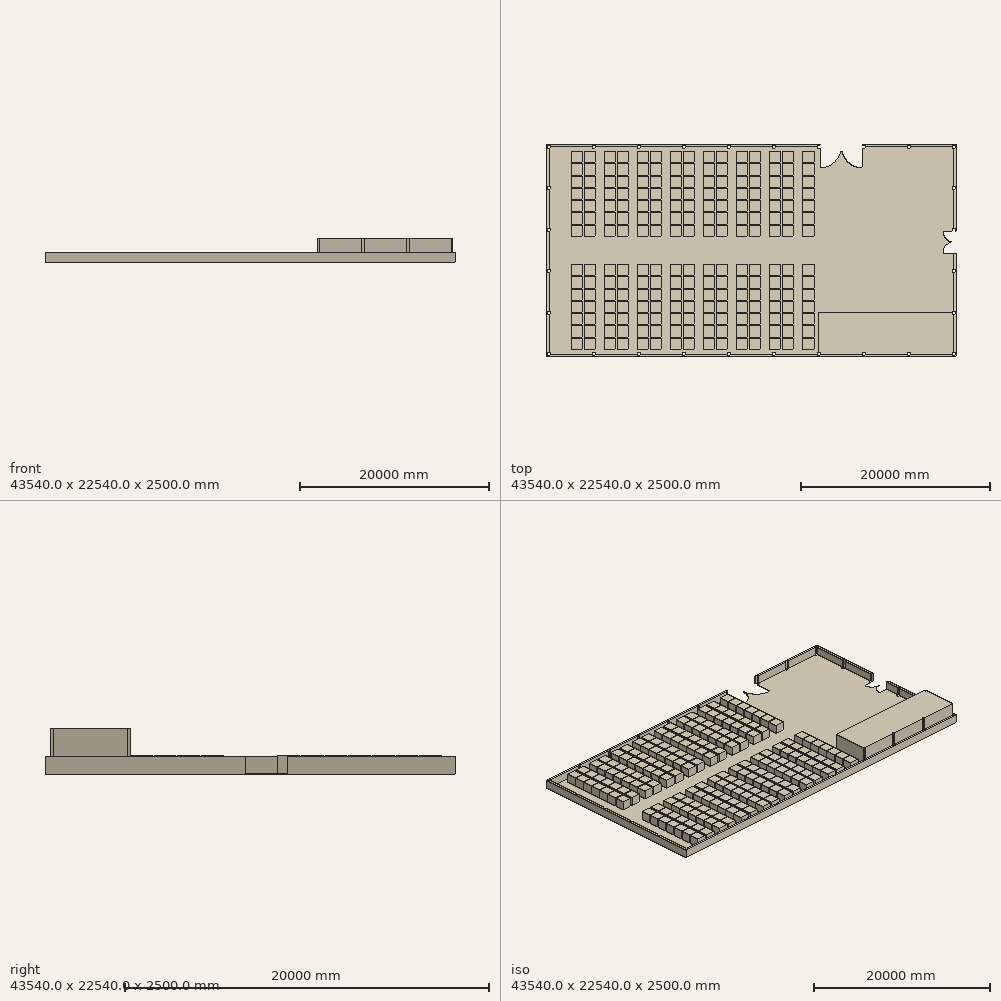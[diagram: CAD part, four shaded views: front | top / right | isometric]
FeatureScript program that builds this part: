
annotation { "Feature Type Name" : "Feature", "Feature Type Description" : "" }
export const myFeature = defineFeature(function(context is Context, id is Id, definition is map)
    precondition{}
    {
        {
            var Q0;
            Q0=qCreatedBy(makeId("Top.planeOp"),FACE);
            var sketch = newSketch(context, id + "F0", { "sketchPlane" : qUnion([Q0])});
            skLineSegment(sketch, "E0", {"start": v(0, 22000) * mm, "end": v(43000, 22000) * mm});
            skLineSegment(sketch, "E1", {"start": v(43000, 22000) * mm, "end": v(43000, 4400) * mm});
            skLineSegment(sketch, "E2", {"start": v(0, 22000) * mm, "end": v(0, 0) * mm});
            skLineSegment(sketch, "E3", {"start": v(0, 0) * mm, "end": v(28666.67, 0) * mm});
            skLineSegment(sketch, "E4.bottom", {"start": v(170, 22170) * mm, "end": v(-170, 22170) * mm});
            skLineSegment(sketch, "E4.top", {"start": v(170, 21830) * mm, "end": v(-170, 21830) * mm});
            skLineSegment(sketch, "E4.left", {"start": v(170, 22170) * mm, "end": v(170, 21830) * mm});
            skLineSegment(sketch, "E4.right", {"start": v(-170, 22170) * mm, "end": v(-170, 21830) * mm});
            skPoint(sketch, "E4.middle", {"position": v(0, 22000) * mm});
            skLineSegment(sketch, "E5.bottom", {"start": v(170, 170) * mm, "end": v(-170, 170) * mm});
            skLineSegment(sketch, "E5.top", {"start": v(170, -170) * mm, "end": v(-170, -170) * mm});
            skLineSegment(sketch, "E5.left", {"start": v(170, 170) * mm, "end": v(170, -170) * mm});
            skLineSegment(sketch, "E5.right", {"start": v(-170, 170) * mm, "end": v(-170, -170) * mm});
            skPoint(sketch, "E5.middle", {"position": v(0, 0) * mm});
            skLineSegment(sketch, "E6.0.1.0", {"start": v(170, 4230) * mm, "end": v(-170, 4230) * mm});
            skLineSegment(sketch, "E6.0.1.1", {"start": v(170, 4570) * mm, "end": v(-170, 4570) * mm});
            skLineSegment(sketch, "E6.0.1.2", {"start": v(170, 4570) * mm, "end": v(170, 4230) * mm});
            skLineSegment(sketch, "E6.0.1.3", {"start": v(-170, 4570) * mm, "end": v(-170, 4230) * mm});
            skLineSegment(sketch, "E6.0.2.0", {"start": v(170, 8630) * mm, "end": v(-170, 8630) * mm});
            skLineSegment(sketch, "E6.0.2.1", {"start": v(170, 8970) * mm, "end": v(-170, 8970) * mm});
            skLineSegment(sketch, "E6.0.2.2", {"start": v(170, 8970) * mm, "end": v(170, 8630) * mm});
            skLineSegment(sketch, "E6.0.2.3", {"start": v(-170, 8970) * mm, "end": v(-170, 8630) * mm});
            skLineSegment(sketch, "E6.0.3.0", {"start": v(170, 13030) * mm, "end": v(-170, 13030) * mm});
            skLineSegment(sketch, "E6.0.3.1", {"start": v(170, 13370) * mm, "end": v(-170, 13370) * mm});
            skLineSegment(sketch, "E6.0.3.2", {"start": v(170, 13370) * mm, "end": v(170, 13030) * mm});
            skLineSegment(sketch, "E6.0.3.3", {"start": v(-170, 13370) * mm, "end": v(-170, 13030) * mm});
            skLineSegment(sketch, "E6.0.4.0", {"start": v(170, 17430) * mm, "end": v(-170, 17430) * mm});
            skLineSegment(sketch, "E6.0.4.1", {"start": v(170, 17770) * mm, "end": v(-170, 17770) * mm});
            skLineSegment(sketch, "E6.0.4.2", {"start": v(170, 17770) * mm, "end": v(170, 17430) * mm});
            skLineSegment(sketch, "E6.0.4.3", {"start": v(-170, 17770) * mm, "end": v(-170, 17430) * mm});
            skLineSegment(sketch, "E7.0.1.0", {"start": v(43170, 4570) * mm, "end": v(43170, 4230) * mm});
            skPoint(sketch, "E7.0.1.1", {"position": v(43000, 4400) * mm});
            skLineSegment(sketch, "E7.0.1.2", {"start": v(42830, 4570) * mm, "end": v(42830, 4230) * mm});
            skLineSegment(sketch, "E7.0.1.4", {"start": v(43170, 4230) * mm, "end": v(42830, 4230) * mm});
            skLineSegment(sketch, "E7.0.1.5", {"start": v(43170, 4570) * mm, "end": v(42830, 4570) * mm});
            skLineSegment(sketch, "E7.0.2.0", {"start": v(43170, 8970) * mm, "end": v(43170, 8630) * mm});
            skPoint(sketch, "E7.0.2.1", {"position": v(43000, 8800) * mm});
            skLineSegment(sketch, "E7.0.2.2", {"start": v(42830, 8970) * mm, "end": v(42830, 8630) * mm});
            skLineSegment(sketch, "E7.0.2.4", {"start": v(43170, 8630) * mm, "end": v(42830, 8630) * mm});
            skLineSegment(sketch, "E7.0.2.5", {"start": v(43170, 8970) * mm, "end": v(42830, 8970) * mm});
            skLineSegment(sketch, "E7.0.3.0", {"start": v(43170, 13370) * mm, "end": v(43170, 13030) * mm});
            skPoint(sketch, "E7.0.3.1", {"position": v(43000, 13200) * mm});
            skLineSegment(sketch, "E7.0.3.2", {"start": v(42830, 13370) * mm, "end": v(42830, 13030) * mm});
            skLineSegment(sketch, "E7.0.3.4", {"start": v(43170, 13030) * mm, "end": v(42830, 13030) * mm});
            skLineSegment(sketch, "E7.0.3.5", {"start": v(43170, 13370) * mm, "end": v(42830, 13370) * mm});
            skLineSegment(sketch, "E7.0.4.0", {"start": v(43170, 17770) * mm, "end": v(43170, 17430) * mm});
            skPoint(sketch, "E7.0.4.1", {"position": v(43000, 17600) * mm});
            skLineSegment(sketch, "E7.0.4.2", {"start": v(42830, 17770) * mm, "end": v(42830, 17430) * mm});
            skLineSegment(sketch, "E7.0.4.4", {"start": v(43170, 17430) * mm, "end": v(42830, 17430) * mm});
            skLineSegment(sketch, "E7.0.4.5", {"start": v(43170, 17770) * mm, "end": v(42830, 17770) * mm});
            skPoint(sketch, "E8.1.0.0", {"position": v(4777.78, 22000) * mm});
            skLineSegment(sketch, "E8.1.0.1", {"start": v(4947.78, 22170) * mm, "end": v(4607.78, 22170) * mm});
            skLineSegment(sketch, "E8.1.0.2", {"start": v(4947.78, 22170) * mm, "end": v(4947.78, 21830) * mm});
            skLineSegment(sketch, "E8.1.0.3", {"start": v(4607.78, 22170) * mm, "end": v(4607.78, 21830) * mm});
            skLineSegment(sketch, "E8.1.0.4", {"start": v(4947.78, 21830) * mm, "end": v(4607.78, 21830) * mm});
            skPoint(sketch, "E8.2.0.0", {"position": v(9555.56, 22000) * mm});
            skLineSegment(sketch, "E8.2.0.1", {"start": v(9725.56, 22170) * mm, "end": v(9385.56, 22170) * mm});
            skLineSegment(sketch, "E8.2.0.2", {"start": v(9725.56, 22170) * mm, "end": v(9725.56, 21830) * mm});
            skLineSegment(sketch, "E8.2.0.3", {"start": v(9385.56, 22170) * mm, "end": v(9385.56, 21830) * mm});
            skLineSegment(sketch, "E8.2.0.4", {"start": v(9725.56, 21830) * mm, "end": v(9385.56, 21830) * mm});
            skPoint(sketch, "E8.3.0.0", {"position": v(14333.33, 22000) * mm});
            skLineSegment(sketch, "E8.3.0.1", {"start": v(14503.33, 22170) * mm, "end": v(14163.33, 22170) * mm});
            skLineSegment(sketch, "E8.3.0.2", {"start": v(14503.33, 22170) * mm, "end": v(14503.33, 21830) * mm});
            skLineSegment(sketch, "E8.3.0.3", {"start": v(14163.33, 22170) * mm, "end": v(14163.33, 21830) * mm});
            skLineSegment(sketch, "E8.3.0.4", {"start": v(14503.33, 21830) * mm, "end": v(14163.33, 21830) * mm});
            skPoint(sketch, "E8.4.0.0", {"position": v(19111.11, 22000) * mm});
            skLineSegment(sketch, "E8.4.0.1", {"start": v(19281.11, 22170) * mm, "end": v(18941.11, 22170) * mm});
            skLineSegment(sketch, "E8.4.0.2", {"start": v(19281.11, 22170) * mm, "end": v(19281.11, 21830) * mm});
            skLineSegment(sketch, "E8.4.0.3", {"start": v(18941.11, 22170) * mm, "end": v(18941.11, 21830) * mm});
            skLineSegment(sketch, "E8.4.0.4", {"start": v(19281.11, 21830) * mm, "end": v(18941.11, 21830) * mm});
            skPoint(sketch, "E8.5.0.0", {"position": v(23888.89, 22000) * mm});
            skLineSegment(sketch, "E8.5.0.1", {"start": v(24058.89, 22170) * mm, "end": v(23718.89, 22170) * mm});
            skLineSegment(sketch, "E8.5.0.2", {"start": v(24058.89, 22170) * mm, "end": v(24058.89, 21830) * mm});
            skLineSegment(sketch, "E8.5.0.3", {"start": v(23718.89, 22170) * mm, "end": v(23718.89, 21830) * mm});
            skLineSegment(sketch, "E8.5.0.4", {"start": v(24058.89, 21830) * mm, "end": v(23718.89, 21830) * mm});
            skPoint(sketch, "E8.6.0.0", {"position": v(28666.67, 22000) * mm});
            skLineSegment(sketch, "E8.6.0.1", {"start": v(28836.67, 22170) * mm, "end": v(28496.67, 22170) * mm});
            skLineSegment(sketch, "E8.6.0.2", {"start": v(28836.67, 22170) * mm, "end": v(28836.67, 21830) * mm});
            skLineSegment(sketch, "E8.6.0.3", {"start": v(28496.67, 22170) * mm, "end": v(28496.67, 21830) * mm});
            skLineSegment(sketch, "E8.6.0.4", {"start": v(28836.67, 21830) * mm, "end": v(28496.67, 21830) * mm});
            skPoint(sketch, "E8.7.0.0", {"position": v(33444.44, 22000) * mm});
            skLineSegment(sketch, "E8.7.0.1", {"start": v(33614.44, 22170) * mm, "end": v(33274.44, 22170) * mm});
            skLineSegment(sketch, "E8.7.0.2", {"start": v(33614.44, 22170) * mm, "end": v(33614.44, 21830) * mm});
            skLineSegment(sketch, "E8.7.0.3", {"start": v(33274.44, 22170) * mm, "end": v(33274.44, 21830) * mm});
            skLineSegment(sketch, "E8.7.0.4", {"start": v(33614.44, 21830) * mm, "end": v(33274.44, 21830) * mm});
            skPoint(sketch, "E8.8.0.0", {"position": v(38222.22, 22000) * mm});
            skLineSegment(sketch, "E8.8.0.1", {"start": v(38392.22, 22170) * mm, "end": v(38052.22, 22170) * mm});
            skLineSegment(sketch, "E8.8.0.2", {"start": v(38392.22, 22170) * mm, "end": v(38392.22, 21830) * mm});
            skLineSegment(sketch, "E8.8.0.3", {"start": v(38052.22, 22170) * mm, "end": v(38052.22, 21830) * mm});
            skLineSegment(sketch, "E8.8.0.4", {"start": v(38392.22, 21830) * mm, "end": v(38052.22, 21830) * mm});
            skPoint(sketch, "E8.9.0.0", {"position": v(43000, 22000) * mm});
            skLineSegment(sketch, "E8.9.0.1", {"start": v(43170, 22170) * mm, "end": v(42830, 22170) * mm});
            skLineSegment(sketch, "E8.9.0.2", {"start": v(43170, 22170) * mm, "end": v(43170, 21830) * mm});
            skLineSegment(sketch, "E8.9.0.3", {"start": v(42830, 22170) * mm, "end": v(42830, 21830) * mm});
            skLineSegment(sketch, "E8.9.0.4", {"start": v(43170, 21830) * mm, "end": v(42830, 21830) * mm});
            skLineSegment(sketch, "E9.1.0.0", {"start": v(4947.78, 170) * mm, "end": v(4607.78, 170) * mm});
            skLineSegment(sketch, "E9.1.0.1", {"start": v(4947.78, -170) * mm, "end": v(4607.78, -170) * mm});
            skPoint(sketch, "E9.1.0.2", {"position": v(4777.78, 0) * mm});
            skLineSegment(sketch, "E9.1.0.3", {"start": v(4607.78, 170) * mm, "end": v(4607.78, -170) * mm});
            skLineSegment(sketch, "E9.1.0.4", {"start": v(4947.78, 170) * mm, "end": v(4947.78, -170) * mm});
            skLineSegment(sketch, "E9.2.0.0", {"start": v(9725.56, 170) * mm, "end": v(9385.56, 170) * mm});
            skLineSegment(sketch, "E9.2.0.1", {"start": v(9725.56, -170) * mm, "end": v(9385.56, -170) * mm});
            skPoint(sketch, "E9.2.0.2", {"position": v(9555.56, 0) * mm});
            skLineSegment(sketch, "E9.2.0.3", {"start": v(9385.56, 170) * mm, "end": v(9385.56, -170) * mm});
            skLineSegment(sketch, "E9.2.0.4", {"start": v(9725.56, 170) * mm, "end": v(9725.56, -170) * mm});
            skLineSegment(sketch, "E9.3.0.0", {"start": v(14503.33, 170) * mm, "end": v(14163.33, 170) * mm});
            skLineSegment(sketch, "E9.3.0.1", {"start": v(14503.33, -170) * mm, "end": v(14163.33, -170) * mm});
            skPoint(sketch, "E9.3.0.2", {"position": v(14333.33, 0) * mm});
            skLineSegment(sketch, "E9.3.0.3", {"start": v(14163.33, 170) * mm, "end": v(14163.33, -170) * mm});
            skLineSegment(sketch, "E9.3.0.4", {"start": v(14503.33, 170) * mm, "end": v(14503.33, -170) * mm});
            skLineSegment(sketch, "E9.4.0.0", {"start": v(19281.11, 170) * mm, "end": v(18941.11, 170) * mm});
            skLineSegment(sketch, "E9.4.0.1", {"start": v(19281.11, -170) * mm, "end": v(18941.11, -170) * mm});
            skPoint(sketch, "E9.4.0.2", {"position": v(19111.11, 0) * mm});
            skLineSegment(sketch, "E9.4.0.3", {"start": v(18941.11, 170) * mm, "end": v(18941.11, -170) * mm});
            skLineSegment(sketch, "E9.4.0.4", {"start": v(19281.11, 170) * mm, "end": v(19281.11, -170) * mm});
            skLineSegment(sketch, "E9.5.0.0", {"start": v(24058.89, 170) * mm, "end": v(23718.89, 170) * mm});
            skLineSegment(sketch, "E9.5.0.1", {"start": v(24058.89, -170) * mm, "end": v(23718.89, -170) * mm});
            skPoint(sketch, "E9.5.0.2", {"position": v(23888.89, 0) * mm});
            skLineSegment(sketch, "E9.5.0.3", {"start": v(23718.89, 170) * mm, "end": v(23718.89, -170) * mm});
            skLineSegment(sketch, "E9.5.0.4", {"start": v(24058.89, 170) * mm, "end": v(24058.89, -170) * mm});
            skLineSegment(sketch, "E9.6.0.0", {"start": v(28836.67, 170) * mm, "end": v(28496.67, 170) * mm});
            skLineSegment(sketch, "E9.6.0.1", {"start": v(28836.67, -170) * mm, "end": v(28496.67, -170) * mm});
            skPoint(sketch, "E9.6.0.2", {"position": v(28666.67, 0) * mm});
            skLineSegment(sketch, "E9.6.0.3", {"start": v(28496.67, 170) * mm, "end": v(28496.67, -170) * mm});
            skLineSegment(sketch, "E9.6.0.4", {"start": v(28836.67, 170) * mm, "end": v(28836.67, -170) * mm});
            skLineSegment(sketch, "E9.7.0.0", {"start": v(33614.44, 170) * mm, "end": v(33274.44, 170) * mm});
            skLineSegment(sketch, "E9.7.0.1", {"start": v(33614.44, -170) * mm, "end": v(33274.44, -170) * mm});
            skPoint(sketch, "E9.7.0.2", {"position": v(33444.44, 0) * mm});
            skLineSegment(sketch, "E9.7.0.3", {"start": v(33274.44, 170) * mm, "end": v(33274.44, -170) * mm});
            skLineSegment(sketch, "E9.7.0.4", {"start": v(33614.44, 170) * mm, "end": v(33614.44, -170) * mm});
            skLineSegment(sketch, "E9.8.0.0", {"start": v(38392.22, 170) * mm, "end": v(38052.22, 170) * mm});
            skLineSegment(sketch, "E9.8.0.1", {"start": v(38392.22, -170) * mm, "end": v(38052.22, -170) * mm});
            skPoint(sketch, "E9.8.0.2", {"position": v(38222.22, 0) * mm});
            skLineSegment(sketch, "E9.8.0.3", {"start": v(38052.22, 170) * mm, "end": v(38052.22, -170) * mm});
            skLineSegment(sketch, "E9.8.0.4", {"start": v(38392.22, 170) * mm, "end": v(38392.22, -170) * mm});
            skLineSegment(sketch, "E9.9.0.0", {"start": v(43170, 170) * mm, "end": v(42830, 170) * mm});
            skLineSegment(sketch, "E9.9.0.1", {"start": v(43170, -170) * mm, "end": v(42830, -170) * mm});
            skPoint(sketch, "E9.9.0.2", {"position": v(43000, 0) * mm});
            skLineSegment(sketch, "E9.9.0.3", {"start": v(42830, 170) * mm, "end": v(42830, -170) * mm});
            skLineSegment(sketch, "E9.9.0.4", {"start": v(43170, 170) * mm, "end": v(43170, -170) * mm});
            skLineSegment(sketch, "E10.bottom", {"start": v(28836.67, 22000) * mm, "end": v(33274.44, 22000) * mm});
            skLineSegment(sketch, "E10.left", {"start": v(28836.67, 22000) * mm, "end": v(28836.67, 19781.11) * mm});
            skLineSegment(sketch, "E10.right", {"start": v(33274.44, 22000) * mm, "end": v(33274.44, 19781.11) * mm});
            skLineSegment(sketch, "E11", {"start": v(28666.67, 0) * mm, "end": v(43000, 0) * mm});
            skLineSegment(sketch, "E12", {"start": v(43000, 4400) * mm, "end": v(43000, 0) * mm});
            skLineSegment(sketch, "E13", {"start": v(43000, 4400) * mm, "end": v(28666.67, 4400) * mm});
            skLineSegment(sketch, "E14", {"start": v(28666.67, 4400) * mm, "end": v(28666.67, 0) * mm});
            skLineSegment(sketch, "E15", {"start": v(33444.44, 0) * mm, "end": v(33444.44, 4400) * mm});
            skLineSegment(sketch, "E16.top", {"start": v(43000, 10730) * mm, "end": v(41850, 10730) * mm});
            skLineSegment(sketch, "E16.left", {"start": v(43000, 13030) * mm, "end": v(43000, 10730) * mm});
            skLineSegment(sketch, "E17.top", {"start": v(69479.6, 14890.56) * mm, "end": v(70779.6, 14890.56) * mm});
            skLineSegment(sketch, "E17.left", {"start": v(69479.6, 17790.56) * mm, "end": v(69479.6, 14890.56) * mm});
            skLineSegment(sketch, "E17.right", {"start": v(70779.6, 17790.56) * mm, "end": v(70779.6, 14890.56) * mm});
            skLineSegment(sketch, "E18", {"start": v(69479.6, 17790.56) * mm, "end": v(69704.6, 17790.56) * mm});
            skLineSegment(sketch, "E19.MirrorCS", {"start": v(69904.6, 17790.56) * mm, "end": v(69904.6, 19390.56) * mm});
            skLineSegment(sketch, "E20", {"start": v(69704.6, 19390.56) * mm, "end": v(69704.6, 17790.56) * mm});
            skLineSegment(sketch, "E21.MirrorCS", {"start": v(70354.6, 17790.56) * mm, "end": v(70354.6, 19390.56) * mm});
            skLineSegment(sketch, "E22.MirrorCS", {"start": v(70554.6, 19390.56) * mm, "end": v(70554.6, 17790.56) * mm});
            skLineSegment(sketch, "E23", {"start": v(69704.6, 19390.56) * mm, "end": v(69904.6, 19390.56) * mm});
            skLineSegment(sketch, "E24.trimOffspring", {"start": v(70354.6, 19390.56) * mm, "end": v(70554.6, 19390.56) * mm});
            skLineSegment(sketch, "E25.bottom", {"start": v(64498.07, 14890.56) * mm, "end": v(65798.07, 14890.56) * mm});
            skLineSegment(sketch, "E25.top", {"start": v(64498.07, 19390.56) * mm, "end": v(65798.07, 19390.56) * mm});
            skLineSegment(sketch, "E25.left", {"start": v(64498.07, 14890.56) * mm, "end": v(64498.07, 19390.56) * mm});
            skLineSegment(sketch, "E25.right", {"start": v(65798.07, 14890.56) * mm, "end": v(65798.07, 19390.56) * mm});
            skLineSegment(sketch, "E26.trimOffspring", {"start": v(69904.6, 17790.56) * mm, "end": v(70354.6, 17790.56) * mm});
            skLineSegment(sketch, "E27.trimOffspring", {"start": v(70554.6, 17790.56) * mm, "end": v(70779.6, 17790.56) * mm});
            skLineSegment(sketch, "E28", {"start": v(30055.67, 19781.11) * mm, "end": v(30055.67, 12000) * mm});
            skLineSegment(sketch, "E29", {"start": v(30055.67, 12000) * mm, "end": v(0, 12000) * mm});
            skLineSegment(sketch, "E30", {"start": v(0, 10000) * mm, "end": v(32055.67, 10000) * mm});
            skLineSegment(sketch, "E31", {"start": v(32055.67, 10000) * mm, "end": v(32055.67, 19781.11) * mm});
            skLineSegment(sketch, "E32", {"start": v(31055.56, 19781.11) * mm, "end": v(31055.56, 11000) * mm, "construction": true});
            skLineSegment(sketch, "E33", {"start": v(31055.56, 11000) * mm, "end": v(0, 11000) * mm, "construction": true});
            skArc(sketch, "E34", {"start": v(43000, 11880) * mm, "mid": v(42186.83, 12216.83) * mm, "end": v(41850, 13030) * mm});
            skLineSegment(sketch, "E35", {"start": v(41850, 13030) * mm, "end": v(43000, 13030) * mm});
            skArc(sketch, "E36", {"start": v(43000, 11880) * mm, "mid": v(42186.83, 11543.17) * mm, "end": v(41850, 10730) * mm});
            skArc(sketch, "E37", {"start": v(31055.56, 22000) * mm, "mid": v(30405.66, 20431) * mm, "end": v(28836.67, 19781.11) * mm});
            skArc(sketch, "E38", {"start": v(31055.56, 22000) * mm, "mid": v(31705.45, 20431) * mm, "end": v(33274.44, 19781.11) * mm});
            skLineSegment(sketch, "E39", {"start": v(28836.67, 19781.11) * mm, "end": v(33274.44, 19781.11) * mm, "construction": true});
            skPoint(sketch, "E40", {"position": v(32055.67, 14890.56) * mm});
            skLineSegment(sketch, "E41", {"start": v(28666.67, 4400) * mm, "end": v(28666.67, 10000) * mm});
            skLineSegment(sketch, "E42.bottom", {"start": v(-270, 22270) * mm, "end": v(43270, 22270) * mm});
            skLineSegment(sketch, "E42.top", {"start": v(-270, -270) * mm, "end": v(43270, -270) * mm});
            skLineSegment(sketch, "E42.left", {"start": v(-270, 22270) * mm, "end": v(-270, -270) * mm});
            skLineSegment(sketch, "E42.right", {"start": v(43270, 22270) * mm, "end": v(43270, -270) * mm});
            skLineSegment(sketch, "E43", {"start": v(33274.44, 22170) * mm, "end": v(33274.44, 22270) * mm});
            skLineSegment(sketch, "E44", {"start": v(28836.67, 22170) * mm, "end": v(28836.67, 22270) * mm});
            skLineSegment(sketch, "E45", {"start": v(43170, 13030) * mm, "end": v(43270, 13030) * mm});
            skLineSegment(sketch, "E46", {"start": v(43000, 10730) * mm, "end": v(43270, 10730) * mm});
            skCircle(sketch, "E47", {"center": v(64985.2, 25566.08) * mm, "radius": 2342 * mm, "construction": true});
            skSolve(sketch);
        }
        {
            var Q0;
            {var subQ15=sQuery(id+"F0.wireOp",EDGE,"E6.0.1.2");Q0=makeQuery(id+"F0.imprint","IMPRINT",FACE,{"disambiguationData":[TD([[makeQuery(id+"F0.imprint","IMPRINT",EDGE,{"derivedFrom":subQ15}),1.0]])]});}
            var Q1;
            {var subQ82=sQuery(id+"F0.wireOp",EDGE,"E6.0.3.2");Q1=makeQuery(id+"F0.imprint","IMPRINT",FACE,{"disambiguationData":[TD([[makeQuery(id+"F0.imprint","IMPRINT",EDGE,{"derivedFrom":subQ82}),1.0]])]});}
            extrude(context, id + "F1", {"entities" : qUnion([Q0, Q1]), "depth" : 25 * mm, "offsetDistance" : 25 * mm});
        }
        {
            var Q0;
            {var subQ0=sQuery(id+"F0.wireOp",EDGE,"Iin0l7VO-2Ex3-duD7-FVRS-qshvhMtlCK30.bottom");Q0=makeQuery(id+"F0.imprint","IMPRINT",FACE,{"disambiguationData":[TD([[makeQuery(id+"F0.imprint","IMPRINT",EDGE,{"derivedFrom":subQ0}),-1.0]])]});}
            var Q1;
            {var subQ3=sQuery(id+"F0.wireOp",EDGE,"HqoQSmvL-XTc1-xB4M-PC8O-pSDQPuOHOdTb.bottom");Q1=makeQuery(id+"F0.imprint","IMPRINT",FACE,{"disambiguationData":[TD([[makeQuery(id+"F0.imprint","IMPRINT",EDGE,{"derivedFrom":subQ3}),-1.0]])]});}
            var Q2;
            Q2=makeQuery(id+"F0.imprint","IMPRINT",FACE,{"disambiguationData":[TD([[makeQuery(id+"F0.imprint","IMPRINT",EDGE,{"derivedFrom":sQuery(id+"F0.wireOp",EDGE,"tGTpAVI9-YHFw-N4Bz-yjAs-Im1oSNZ9DJVB.bottom")}),-1.0]])]});
            var Q3;
            Q3=makeQuery(id+"F0.imprint","IMPRINT",FACE,{"disambiguationData":[TD([[makeQuery(id+"F0.imprint","IMPRINT",EDGE,{"derivedFrom":sQuery(id+"F0.wireOp",EDGE,"TcqQWqTF-7XCL-TTZD-UDu0-ZkwaWHukuYan.bottom")}),-1.0]])]});
            var Q4;
            Q4=makeQuery(id+"F0.imprint","IMPRINT",FACE,{"disambiguationData":[TD([[makeQuery(id+"F0.imprint","IMPRINT",EDGE,{"derivedFrom":sQuery(id+"F0.wireOp",EDGE,"2tnjIj2e-qudf-ib6D-KHT0-7kGwBXjBkbSC.bottom")}),-1.0]])]});
            var Q5;
            {var subQ11=sQuery(id+"F0.wireOp",EDGE,"E9.8.0.0");Q5=makeQuery(id+"F0.imprint","IMPRINT",FACE,{"disambiguationData":[TD([[makeQuery(id+"F0.imprint","IMPRINT",EDGE,{"derivedFrom":subQ11}),-1.0]])]});}
            extrude(context, id + "F2", {"entities" : qUnion([Q0, Q1, Q2, Q3, Q4, Q5]), "depth" : 2500 * mm, "offsetDistance" : 25 * mm});
        }
        {
            var Q0;
            {var subQ7=sQuery(id+"F0.wireOp",EDGE,"E9.6.0.4");var subQ8=sQuery(id+"F0.wireOp",EDGE,"E9.6.0.0");var subQ9=makeQuery(id+"F0.imprint","INTERSECT",VERTEX,{"derivedFrom":[subQ8,subQ7]});Q0=makeQuery(id+"F0.imprint","IMPRINT",FACE,{"disambiguationData":[TD([[makeQuery(id+"F0.imprint","IMPRINT",EDGE,{"disambiguationData":[TD([[subQ9,-1.0]])],"derivedFrom":subQ8}),-1.0]])]});}
            extrude(context, id + "F3", {"entities" : qUnion([Q0]), "depth" : 2500 * mm, "offsetDistance" : 25 * mm});
        }
        {
            var Q0;
            {var subQ110=sQuery(id+"F0.wireOp",EDGE,"E4.bottom");Q0=makeQuery(id+"F0.imprint","IMPRINT",FACE,{"disambiguationData":[TD([[makeQuery(id+"F0.imprint","IMPRINT",EDGE,{"derivedFrom":subQ110}),-1.0]])]});}
            var Q1;
            {var subQ7=sQuery(id+"F0.wireOp",EDGE,"E7.0.3.0");Q1=makeQuery(id+"F0.imprint","IMPRINT",FACE,{"disambiguationData":[TD([[makeQuery(id+"F0.imprint","IMPRINT",EDGE,{"derivedFrom":subQ7}),1.0]])]});}
            extrude(context, id + "F4", {"entities" : qUnion([Q0, Q1]), "operationType" : NewBodyOperationType.ADD, "depth" : 1000 * mm, "offsetDistance" : 25 * mm});
        }
        {
            var Q0;
            Q0=makeQuery(id+"F1.opExtrude","CAP_FACE",FACE,{"disambiguationData":[OSD([sQuery(id+"F0.wireOp",EDGE,"E0"),sQuery(id+"F0.wireOp",EDGE,"E1"),sQuery(id+"F0.wireOp",EDGE,"E2"),sQuery(id+"F0.wireOp",EDGE,"E3"),sQuery(id+"F0.wireOp",EDGE,"E4.top"),sQuery(id+"F0.wireOp",EDGE,"E4.left"),sQuery(id+"F0.wireOp",EDGE,"E5.bottom"),sQuery(id+"F0.wireOp",EDGE,"E5.left"),sQuery(id+"F0.wireOp",EDGE,"E6.0.1.0"),sQuery(id+"F0.wireOp",EDGE,"E6.0.1.1"),sQuery(id+"F0.wireOp",EDGE,"E6.0.1.2"),sQuery(id+"F0.wireOp",EDGE,"E6.0.2.0"),sQuery(id+"F0.wireOp",EDGE,"E6.0.2.1"),sQuery(id+"F0.wireOp",EDGE,"E6.0.2.2"),sQuery(id+"F0.wireOp",EDGE,"E6.0.3.0"),sQuery(id+"F0.wireOp",EDGE,"E6.0.3.1"),sQuery(id+"F0.wireOp",EDGE,"E6.0.3.2"),sQuery(id+"F0.wireOp",EDGE,"E6.0.4.0"),sQuery(id+"F0.wireOp",EDGE,"E6.0.4.1"),sQuery(id+"F0.wireOp",EDGE,"E6.0.4.2"),sQuery(id+"F0.wireOp",EDGE,"E7.0.1.2"),sQuery(id+"F0.wireOp",EDGE,"E7.0.1.5"),sQuery(id+"F0.wireOp",EDGE,"E7.0.2.2"),sQuery(id+"F0.wireOp",EDGE,"E7.0.2.4"),sQuery(id+"F0.wireOp",EDGE,"E7.0.2.5"),sQuery(id+"F0.wireOp",EDGE,"E7.0.3.2"),sQuery(id+"F0.wireOp",EDGE,"E7.0.3.5"),sQuery(id+"F0.wireOp",EDGE,"E7.0.4.2"),sQuery(id+"F0.wireOp",EDGE,"E7.0.4.4"),sQuery(id+"F0.wireOp",EDGE,"E7.0.4.5"),sQuery(id+"F0.wireOp",EDGE,"E8.1.0.2"),sQuery(id+"F0.wireOp",EDGE,"E8.1.0.3"),sQuery(id+"F0.wireOp",EDGE,"E8.1.0.4"),sQuery(id+"F0.wireOp",EDGE,"E8.2.0.2"),sQuery(id+"F0.wireOp",EDGE,"E8.2.0.3"),sQuery(id+"F0.wireOp",EDGE,"E8.2.0.4"),sQuery(id+"F0.wireOp",EDGE,"E8.3.0.2"),sQuery(id+"F0.wireOp",EDGE,"E8.3.0.3"),sQuery(id+"F0.wireOp",EDGE,"E8.3.0.4"),sQuery(id+"F0.wireOp",EDGE,"E8.4.0.2"),sQuery(id+"F0.wireOp",EDGE,"E8.4.0.3"),sQuery(id+"F0.wireOp",EDGE,"E8.4.0.4"),sQuery(id+"F0.wireOp",EDGE,"E8.5.0.2"),sQuery(id+"F0.wireOp",EDGE,"E8.5.0.3"),sQuery(id+"F0.wireOp",EDGE,"E8.5.0.4"),sQuery(id+"F0.wireOp",EDGE,"E8.6.0.3"),sQuery(id+"F0.wireOp",EDGE,"E8.6.0.4"),sQuery(id+"F0.wireOp",EDGE,"E8.7.0.2"),sQuery(id+"F0.wireOp",EDGE,"E8.7.0.4"),sQuery(id+"F0.wireOp",EDGE,"E8.8.0.2"),sQuery(id+"F0.wireOp",EDGE,"E8.8.0.3"),sQuery(id+"F0.wireOp",EDGE,"E8.8.0.4"),sQuery(id+"F0.wireOp",EDGE,"E8.9.0.3"),sQuery(id+"F0.wireOp",EDGE,"E8.9.0.4"),sQuery(id+"F0.wireOp",EDGE,"E9.1.0.0"),sQuery(id+"F0.wireOp",EDGE,"E9.1.0.3"),sQuery(id+"F0.wireOp",EDGE,"E9.1.0.4"),sQuery(id+"F0.wireOp",EDGE,"E9.2.0.0"),sQuery(id+"F0.wireOp",EDGE,"E9.2.0.3"),sQuery(id+"F0.wireOp",EDGE,"E9.2.0.4"),sQuery(id+"F0.wireOp",EDGE,"E9.3.0.0"),sQuery(id+"F0.wireOp",EDGE,"E9.3.0.3"),sQuery(id+"F0.wireOp",EDGE,"E9.3.0.4"),sQuery(id+"F0.wireOp",EDGE,"E9.4.0.0"),sQuery(id+"F0.wireOp",EDGE,"E9.4.0.3"),sQuery(id+"F0.wireOp",EDGE,"E9.4.0.4"),sQuery(id+"F0.wireOp",EDGE,"E9.5.0.0"),sQuery(id+"F0.wireOp",EDGE,"E9.5.0.3"),sQuery(id+"F0.wireOp",EDGE,"E9.5.0.4"),sQuery(id+"F0.wireOp",EDGE,"E9.6.0.0"),sQuery(id+"F0.wireOp",EDGE,"E9.6.0.3"),sQuery(id+"F0.wireOp",EDGE,"E10.left"),sQuery(id+"F0.wireOp",EDGE,"E10.right"),sQuery(id+"F0.wireOp",EDGE,"E13"),sQuery(id+"F0.wireOp",EDGE,"E14"),sQuery(id+"F0.wireOp",EDGE,"E16.top"),sQuery(id+"F0.wireOp",EDGE,"E34"),sQuery(id+"F0.wireOp",EDGE,"E35"),sQuery(id+"F0.wireOp",EDGE,"E36"),sQuery(id+"F0.wireOp",EDGE,"E37"),sQuery(id+"F0.wireOp",EDGE,"E38")])],"isStart":false});
            var sketch = newSketch(context, id + "F5", { "sketchPlane" : qUnion([Q0])});
            skLineSegment(sketch, "E48.bottom", {"start": v(28166.67, 500) * mm, "end": v(26966.67, 500) * mm});
            skLineSegment(sketch, "E48.top", {"start": v(28166.67, 1700) * mm, "end": v(26966.67, 1700) * mm});
            skLineSegment(sketch, "E48.left", {"start": v(28166.67, 500) * mm, "end": v(28166.67, 1700) * mm});
            skLineSegment(sketch, "E48.right", {"start": v(26966.67, 500) * mm, "end": v(26966.67, 1700) * mm});
            skLineSegment(sketch, "E49.0.1.0", {"start": v(28166.67, 3000) * mm, "end": v(26966.67, 3000) * mm});
            skLineSegment(sketch, "E49.0.1.1", {"start": v(26966.67, 1800) * mm, "end": v(26966.67, 3000) * mm});
            skLineSegment(sketch, "E49.0.1.2", {"start": v(28166.67, 1800) * mm, "end": v(26966.67, 1800) * mm});
            skLineSegment(sketch, "E49.0.1.3", {"start": v(28166.67, 1800) * mm, "end": v(28166.67, 3000) * mm});
            skLineSegment(sketch, "E49.0.2.0", {"start": v(28166.67, 4300) * mm, "end": v(26966.67, 4300) * mm});
            skLineSegment(sketch, "E49.0.2.1", {"start": v(26966.67, 3100) * mm, "end": v(26966.67, 4300) * mm});
            skLineSegment(sketch, "E49.0.2.2", {"start": v(28166.67, 3100) * mm, "end": v(26966.67, 3100) * mm});
            skLineSegment(sketch, "E49.0.2.3", {"start": v(28166.67, 3100) * mm, "end": v(28166.67, 4300) * mm});
            skLineSegment(sketch, "E49.0.3.0", {"start": v(28166.67, 5600) * mm, "end": v(26966.67, 5600) * mm});
            skLineSegment(sketch, "E49.0.3.1", {"start": v(26966.67, 4400) * mm, "end": v(26966.67, 5600) * mm});
            skLineSegment(sketch, "E49.0.3.2", {"start": v(28166.67, 4400) * mm, "end": v(26966.67, 4400) * mm});
            skLineSegment(sketch, "E49.0.3.3", {"start": v(28166.67, 4400) * mm, "end": v(28166.67, 5600) * mm});
            skLineSegment(sketch, "E49.0.4.0", {"start": v(28166.67, 6900) * mm, "end": v(26966.67, 6900) * mm});
            skLineSegment(sketch, "E49.0.4.1", {"start": v(26966.67, 5700) * mm, "end": v(26966.67, 6900) * mm});
            skLineSegment(sketch, "E49.0.4.2", {"start": v(28166.67, 5700) * mm, "end": v(26966.67, 5700) * mm});
            skLineSegment(sketch, "E49.0.4.3", {"start": v(28166.67, 5700) * mm, "end": v(28166.67, 6900) * mm});
            skLineSegment(sketch, "E49.0.5.0", {"start": v(28166.67, 8200) * mm, "end": v(26966.67, 8200) * mm});
            skLineSegment(sketch, "E49.0.5.1", {"start": v(26966.67, 7000) * mm, "end": v(26966.67, 8200) * mm});
            skLineSegment(sketch, "E49.0.5.2", {"start": v(28166.67, 7000) * mm, "end": v(26966.67, 7000) * mm});
            skLineSegment(sketch, "E49.0.5.3", {"start": v(28166.67, 7000) * mm, "end": v(28166.67, 8200) * mm});
            skLineSegment(sketch, "E49.0.6.0", {"start": v(28166.67, 9500) * mm, "end": v(26966.67, 9500) * mm});
            skLineSegment(sketch, "E49.0.6.1", {"start": v(26966.67, 8300) * mm, "end": v(26966.67, 9500) * mm});
            skLineSegment(sketch, "E49.0.6.2", {"start": v(28166.67, 8300) * mm, "end": v(26966.67, 8300) * mm});
            skLineSegment(sketch, "E49.0.6.3", {"start": v(28166.67, 8300) * mm, "end": v(28166.67, 9500) * mm});
            skLineSegment(sketch, "E49.direction1", {"start": v(26966.67, 1700) * mm, "end": v(27932.88, 1700) * mm, "construction": true});
            skLineSegment(sketch, "E49.direction2", {"start": v(26966.67, 1700) * mm, "end": v(26966.67, 3000) * mm, "construction": true});
            skLineSegment(sketch, "E50.bottom", {"start": v(25966.67, 500) * mm, "end": v(24766.67, 500) * mm});
            skLineSegment(sketch, "E50.top", {"start": v(25966.67, 1700) * mm, "end": v(24766.67, 1700) * mm});
            skLineSegment(sketch, "E50.left", {"start": v(25966.67, 500) * mm, "end": v(25966.67, 1700) * mm});
            skLineSegment(sketch, "E50.right", {"start": v(24766.67, 500) * mm, "end": v(24766.67, 1700) * mm});
            skLineSegment(sketch, "E51.bottom", {"start": v(24566.67, 500) * mm, "end": v(23366.67, 500) * mm});
            skLineSegment(sketch, "E51.top", {"start": v(24566.67, 1700) * mm, "end": v(23366.67, 1700) * mm});
            skLineSegment(sketch, "E51.left", {"start": v(24566.67, 500) * mm, "end": v(24566.67, 1700) * mm});
            skLineSegment(sketch, "E51.right", {"start": v(23366.67, 500) * mm, "end": v(23366.67, 1700) * mm});
            skLineSegment(sketch, "E52.1.0.0", {"start": v(22466.67, 500) * mm, "end": v(22466.67, 1700) * mm});
            skLineSegment(sketch, "E52.1.0.1", {"start": v(21066.67, 500) * mm, "end": v(19866.67, 500) * mm});
            skLineSegment(sketch, "E52.1.0.2", {"start": v(21066.67, 1700) * mm, "end": v(19866.67, 1700) * mm});
            skLineSegment(sketch, "E52.1.0.3", {"start": v(19866.67, 500) * mm, "end": v(19866.67, 1700) * mm});
            skLineSegment(sketch, "E52.1.0.4", {"start": v(21266.67, 500) * mm, "end": v(21266.67, 1700) * mm});
            skLineSegment(sketch, "E52.1.0.5", {"start": v(21066.67, 500) * mm, "end": v(21066.67, 1700) * mm});
            skLineSegment(sketch, "E52.1.0.6", {"start": v(22466.67, 500) * mm, "end": v(21266.67, 500) * mm});
            skLineSegment(sketch, "E52.1.0.7", {"start": v(22466.67, 1700) * mm, "end": v(21266.67, 1700) * mm});
            skLineSegment(sketch, "E52.2.0.0", {"start": v(18966.67, 500) * mm, "end": v(18966.67, 1700) * mm});
            skLineSegment(sketch, "E52.2.0.1", {"start": v(17566.67, 500) * mm, "end": v(16366.67, 500) * mm});
            skLineSegment(sketch, "E52.2.0.2", {"start": v(17566.67, 1700) * mm, "end": v(16366.67, 1700) * mm});
            skLineSegment(sketch, "E52.2.0.3", {"start": v(16366.67, 500) * mm, "end": v(16366.67, 1700) * mm});
            skLineSegment(sketch, "E52.2.0.4", {"start": v(17766.67, 500) * mm, "end": v(17766.67, 1700) * mm});
            skLineSegment(sketch, "E52.2.0.5", {"start": v(17566.67, 500) * mm, "end": v(17566.67, 1700) * mm});
            skLineSegment(sketch, "E52.2.0.6", {"start": v(18966.67, 500) * mm, "end": v(17766.67, 500) * mm});
            skLineSegment(sketch, "E52.2.0.7", {"start": v(18966.67, 1700) * mm, "end": v(17766.67, 1700) * mm});
            skLineSegment(sketch, "E52.3.0.0", {"start": v(15466.67, 500) * mm, "end": v(15466.67, 1700) * mm});
            skLineSegment(sketch, "E52.3.0.1", {"start": v(14066.67, 500) * mm, "end": v(12866.67, 500) * mm});
            skLineSegment(sketch, "E52.3.0.2", {"start": v(14066.67, 1700) * mm, "end": v(12866.67, 1700) * mm});
            skLineSegment(sketch, "E52.3.0.3", {"start": v(12866.67, 500) * mm, "end": v(12866.67, 1700) * mm});
            skLineSegment(sketch, "E52.3.0.4", {"start": v(14266.67, 500) * mm, "end": v(14266.67, 1700) * mm});
            skLineSegment(sketch, "E52.3.0.5", {"start": v(14066.67, 500) * mm, "end": v(14066.67, 1700) * mm});
            skLineSegment(sketch, "E52.3.0.6", {"start": v(15466.67, 500) * mm, "end": v(14266.67, 500) * mm});
            skLineSegment(sketch, "E52.3.0.7", {"start": v(15466.67, 1700) * mm, "end": v(14266.67, 1700) * mm});
            skLineSegment(sketch, "E52.4.0.0", {"start": v(11966.67, 500) * mm, "end": v(11966.67, 1700) * mm});
            skLineSegment(sketch, "E52.4.0.1", {"start": v(10566.67, 500) * mm, "end": v(9366.67, 500) * mm});
            skLineSegment(sketch, "E52.4.0.2", {"start": v(10566.67, 1700) * mm, "end": v(9366.67, 1700) * mm});
            skLineSegment(sketch, "E52.4.0.3", {"start": v(9366.67, 500) * mm, "end": v(9366.67, 1700) * mm});
            skLineSegment(sketch, "E52.4.0.4", {"start": v(10766.67, 500) * mm, "end": v(10766.67, 1700) * mm});
            skLineSegment(sketch, "E52.4.0.5", {"start": v(10566.67, 500) * mm, "end": v(10566.67, 1700) * mm});
            skLineSegment(sketch, "E52.4.0.6", {"start": v(11966.67, 500) * mm, "end": v(10766.67, 500) * mm});
            skLineSegment(sketch, "E52.4.0.7", {"start": v(11966.67, 1700) * mm, "end": v(10766.67, 1700) * mm});
            skLineSegment(sketch, "E52.5.0.0", {"start": v(8466.67, 500) * mm, "end": v(8466.67, 1700) * mm});
            skLineSegment(sketch, "E52.5.0.1", {"start": v(7066.67, 500) * mm, "end": v(5866.67, 500) * mm});
            skLineSegment(sketch, "E52.5.0.2", {"start": v(7066.67, 1700) * mm, "end": v(5866.67, 1700) * mm});
            skLineSegment(sketch, "E52.5.0.3", {"start": v(5866.67, 500) * mm, "end": v(5866.67, 1700) * mm});
            skLineSegment(sketch, "E52.5.0.4", {"start": v(7266.67, 500) * mm, "end": v(7266.67, 1700) * mm});
            skLineSegment(sketch, "E52.5.0.5", {"start": v(7066.67, 500) * mm, "end": v(7066.67, 1700) * mm});
            skLineSegment(sketch, "E52.5.0.6", {"start": v(8466.67, 500) * mm, "end": v(7266.67, 500) * mm});
            skLineSegment(sketch, "E52.5.0.7", {"start": v(8466.67, 1700) * mm, "end": v(7266.67, 1700) * mm});
            skLineSegment(sketch, "E52.6.0.0", {"start": v(4966.67, 500) * mm, "end": v(4966.67, 1700) * mm});
            skLineSegment(sketch, "E52.6.0.1", {"start": v(3566.67, 500) * mm, "end": v(2366.67, 500) * mm});
            skLineSegment(sketch, "E52.6.0.2", {"start": v(3566.67, 1700) * mm, "end": v(2366.67, 1700) * mm});
            skLineSegment(sketch, "E52.6.0.3", {"start": v(2366.67, 500) * mm, "end": v(2366.67, 1700) * mm});
            skLineSegment(sketch, "E52.6.0.4", {"start": v(3766.67, 500) * mm, "end": v(3766.67, 1700) * mm});
            skLineSegment(sketch, "E52.6.0.5", {"start": v(3566.67, 500) * mm, "end": v(3566.67, 1700) * mm});
            skLineSegment(sketch, "E52.6.0.6", {"start": v(4966.67, 500) * mm, "end": v(3766.67, 500) * mm});
            skLineSegment(sketch, "E52.6.0.7", {"start": v(4966.67, 1700) * mm, "end": v(3766.67, 1700) * mm});
            skLineSegment(sketch, "E52.direction1", {"start": v(23366.67, 500) * mm, "end": v(19866.67, 500) * mm, "construction": true});
            skLineSegment(sketch, "E53.0.1.0", {"start": v(18966.67, 1800) * mm, "end": v(18966.67, 3000) * mm});
            skLineSegment(sketch, "E53.0.1.1", {"start": v(23366.67, 1800) * mm, "end": v(23366.67, 3000) * mm});
            skLineSegment(sketch, "E53.0.1.2", {"start": v(24566.67, 3000) * mm, "end": v(23366.67, 3000) * mm});
            skLineSegment(sketch, "E53.0.1.3", {"start": v(15466.67, 1800) * mm, "end": v(14266.67, 1800) * mm});
            skLineSegment(sketch, "E53.0.1.4", {"start": v(2366.67, 1800) * mm, "end": v(2366.67, 3000) * mm});
            skLineSegment(sketch, "E53.0.1.5", {"start": v(24566.67, 1800) * mm, "end": v(23366.67, 1800) * mm});
            skLineSegment(sketch, "E53.0.1.6", {"start": v(14066.67, 1800) * mm, "end": v(12866.67, 1800) * mm});
            skLineSegment(sketch, "E53.0.1.7", {"start": v(10566.67, 1800) * mm, "end": v(9366.67, 1800) * mm});
            skLineSegment(sketch, "E53.0.1.8", {"start": v(11966.67, 1800) * mm, "end": v(11966.67, 3000) * mm});
            skLineSegment(sketch, "E53.0.1.9", {"start": v(25966.67, 1800) * mm, "end": v(25966.67, 3000) * mm});
            skLineSegment(sketch, "E53.0.1.10", {"start": v(7066.67, 3000) * mm, "end": v(5866.67, 3000) * mm});
            skLineSegment(sketch, "E53.0.1.11", {"start": v(17566.67, 1800) * mm, "end": v(16366.67, 1800) * mm});
            skLineSegment(sketch, "E53.0.1.12", {"start": v(10566.67, 3000) * mm, "end": v(9366.67, 3000) * mm});
            skLineSegment(sketch, "E53.0.1.13", {"start": v(25966.67, 1800) * mm, "end": v(24766.67, 1800) * mm});
            skLineSegment(sketch, "E53.0.1.14", {"start": v(14066.67, 1800) * mm, "end": v(14066.67, 3000) * mm});
            skLineSegment(sketch, "E53.0.1.15", {"start": v(16366.67, 1800) * mm, "end": v(16366.67, 3000) * mm});
            skLineSegment(sketch, "E53.0.1.16", {"start": v(8466.67, 1800) * mm, "end": v(8466.67, 3000) * mm});
            skLineSegment(sketch, "E53.0.1.17", {"start": v(21066.67, 1800) * mm, "end": v(21066.67, 3000) * mm});
            skLineSegment(sketch, "E53.0.1.18", {"start": v(22466.67, 1800) * mm, "end": v(22466.67, 3000) * mm});
            skLineSegment(sketch, "E53.0.1.19", {"start": v(21066.67, 3000) * mm, "end": v(19866.67, 3000) * mm});
            skLineSegment(sketch, "E53.0.1.20", {"start": v(3566.67, 1800) * mm, "end": v(3566.67, 3000) * mm});
            skLineSegment(sketch, "E53.0.1.21", {"start": v(14066.67, 3000) * mm, "end": v(12866.67, 3000) * mm});
            skLineSegment(sketch, "E53.0.1.22", {"start": v(9366.67, 1800) * mm, "end": v(9366.67, 3000) * mm});
            skLineSegment(sketch, "E53.0.1.23", {"start": v(10566.67, 1800) * mm, "end": v(10566.67, 3000) * mm});
            skLineSegment(sketch, "E53.0.1.24", {"start": v(3566.67, 1800) * mm, "end": v(2366.67, 1800) * mm});
            skLineSegment(sketch, "E53.0.1.25", {"start": v(25966.67, 3000) * mm, "end": v(24766.67, 3000) * mm});
            skLineSegment(sketch, "E53.0.1.26", {"start": v(22466.67, 3000) * mm, "end": v(21266.67, 3000) * mm});
            skLineSegment(sketch, "E53.0.1.27", {"start": v(15466.67, 1800) * mm, "end": v(15466.67, 3000) * mm});
            skLineSegment(sketch, "E53.0.1.28", {"start": v(18966.67, 1800) * mm, "end": v(17766.67, 1800) * mm});
            skLineSegment(sketch, "E53.0.1.29", {"start": v(24566.67, 1800) * mm, "end": v(24566.67, 3000) * mm});
            skLineSegment(sketch, "E53.0.1.30", {"start": v(24766.67, 1800) * mm, "end": v(24766.67, 3000) * mm});
            skLineSegment(sketch, "E53.0.1.31", {"start": v(5866.67, 1800) * mm, "end": v(5866.67, 3000) * mm});
            skLineSegment(sketch, "E53.0.1.32", {"start": v(18966.67, 3000) * mm, "end": v(17766.67, 3000) * mm});
            skLineSegment(sketch, "E53.0.1.33", {"start": v(8466.67, 3000) * mm, "end": v(7266.67, 3000) * mm});
            skLineSegment(sketch, "E53.0.1.34", {"start": v(11966.67, 1800) * mm, "end": v(10766.67, 1800) * mm});
            skLineSegment(sketch, "E53.0.1.35", {"start": v(3566.67, 3000) * mm, "end": v(2366.67, 3000) * mm});
            skLineSegment(sketch, "E53.0.1.36", {"start": v(10766.67, 1800) * mm, "end": v(10766.67, 3000) * mm});
            skLineSegment(sketch, "E53.0.1.37", {"start": v(4966.67, 1800) * mm, "end": v(4966.67, 3000) * mm});
            skLineSegment(sketch, "E53.0.1.38", {"start": v(3766.67, 1800) * mm, "end": v(3766.67, 3000) * mm});
            skLineSegment(sketch, "E53.0.1.39", {"start": v(17766.67, 1800) * mm, "end": v(17766.67, 3000) * mm});
            skLineSegment(sketch, "E53.0.1.40", {"start": v(17566.67, 3000) * mm, "end": v(16366.67, 3000) * mm});
            skLineSegment(sketch, "E53.0.1.41", {"start": v(4966.67, 3000) * mm, "end": v(3766.67, 3000) * mm});
            skLineSegment(sketch, "E53.0.1.42", {"start": v(23366.67, 1800) * mm, "end": v(19866.67, 1800) * mm, "construction": true});
            skLineSegment(sketch, "E53.0.1.43", {"start": v(15466.67, 3000) * mm, "end": v(14266.67, 3000) * mm});
            skLineSegment(sketch, "E53.0.1.44", {"start": v(17566.67, 1800) * mm, "end": v(17566.67, 3000) * mm});
            skLineSegment(sketch, "E53.0.1.45", {"start": v(4966.67, 1800) * mm, "end": v(3766.67, 1800) * mm});
            skLineSegment(sketch, "E53.0.1.46", {"start": v(8466.67, 1800) * mm, "end": v(7266.67, 1800) * mm});
            skLineSegment(sketch, "E53.0.1.47", {"start": v(11966.67, 3000) * mm, "end": v(10766.67, 3000) * mm});
            skLineSegment(sketch, "E53.0.1.48", {"start": v(14266.67, 1800) * mm, "end": v(14266.67, 3000) * mm});
            skLineSegment(sketch, "E53.0.1.49", {"start": v(21266.67, 1800) * mm, "end": v(21266.67, 3000) * mm});
            skLineSegment(sketch, "E53.0.1.50", {"start": v(7066.67, 1800) * mm, "end": v(7066.67, 3000) * mm});
            skLineSegment(sketch, "E53.0.1.51", {"start": v(7066.67, 1800) * mm, "end": v(5866.67, 1800) * mm});
            skLineSegment(sketch, "E53.0.1.52", {"start": v(12866.67, 1800) * mm, "end": v(12866.67, 3000) * mm});
            skLineSegment(sketch, "E53.0.1.53", {"start": v(19866.67, 1800) * mm, "end": v(19866.67, 3000) * mm});
            skLineSegment(sketch, "E53.0.1.54", {"start": v(7266.67, 1800) * mm, "end": v(7266.67, 3000) * mm});
            skLineSegment(sketch, "E53.0.1.55", {"start": v(22466.67, 1800) * mm, "end": v(21266.67, 1800) * mm});
            skLineSegment(sketch, "E53.0.1.56", {"start": v(21066.67, 1800) * mm, "end": v(19866.67, 1800) * mm});
            skLineSegment(sketch, "E53.0.2.0", {"start": v(18966.67, 3100) * mm, "end": v(18966.67, 4300) * mm});
            skLineSegment(sketch, "E53.0.2.1", {"start": v(23366.67, 3100) * mm, "end": v(23366.67, 4300) * mm});
            skLineSegment(sketch, "E53.0.2.2", {"start": v(24566.67, 4300) * mm, "end": v(23366.67, 4300) * mm});
            skLineSegment(sketch, "E53.0.2.3", {"start": v(15466.67, 3100) * mm, "end": v(14266.67, 3100) * mm});
            skLineSegment(sketch, "E53.0.2.4", {"start": v(2366.67, 3100) * mm, "end": v(2366.67, 4300) * mm});
            skLineSegment(sketch, "E53.0.2.5", {"start": v(24566.67, 3100) * mm, "end": v(23366.67, 3100) * mm});
            skLineSegment(sketch, "E53.0.2.6", {"start": v(14066.67, 3100) * mm, "end": v(12866.67, 3100) * mm});
            skLineSegment(sketch, "E53.0.2.7", {"start": v(10566.67, 3100) * mm, "end": v(9366.67, 3100) * mm});
            skLineSegment(sketch, "E53.0.2.8", {"start": v(11966.67, 3100) * mm, "end": v(11966.67, 4300) * mm});
            skLineSegment(sketch, "E53.0.2.9", {"start": v(25966.67, 3100) * mm, "end": v(25966.67, 4300) * mm});
            skLineSegment(sketch, "E53.0.2.10", {"start": v(7066.67, 4300) * mm, "end": v(5866.67, 4300) * mm});
            skLineSegment(sketch, "E53.0.2.11", {"start": v(17566.67, 3100) * mm, "end": v(16366.67, 3100) * mm});
            skLineSegment(sketch, "E53.0.2.12", {"start": v(10566.67, 4300) * mm, "end": v(9366.67, 4300) * mm});
            skLineSegment(sketch, "E53.0.2.13", {"start": v(25966.67, 3100) * mm, "end": v(24766.67, 3100) * mm});
            skLineSegment(sketch, "E53.0.2.14", {"start": v(14066.67, 3100) * mm, "end": v(14066.67, 4300) * mm});
            skLineSegment(sketch, "E53.0.2.15", {"start": v(16366.67, 3100) * mm, "end": v(16366.67, 4300) * mm});
            skLineSegment(sketch, "E53.0.2.16", {"start": v(8466.67, 3100) * mm, "end": v(8466.67, 4300) * mm});
            skLineSegment(sketch, "E53.0.2.17", {"start": v(21066.67, 3100) * mm, "end": v(21066.67, 4300) * mm});
            skLineSegment(sketch, "E53.0.2.18", {"start": v(22466.67, 3100) * mm, "end": v(22466.67, 4300) * mm});
            skLineSegment(sketch, "E53.0.2.19", {"start": v(21066.67, 4300) * mm, "end": v(19866.67, 4300) * mm});
            skLineSegment(sketch, "E53.0.2.20", {"start": v(3566.67, 3100) * mm, "end": v(3566.67, 4300) * mm});
            skLineSegment(sketch, "E53.0.2.21", {"start": v(14066.67, 4300) * mm, "end": v(12866.67, 4300) * mm});
            skLineSegment(sketch, "E53.0.2.22", {"start": v(9366.67, 3100) * mm, "end": v(9366.67, 4300) * mm});
            skLineSegment(sketch, "E53.0.2.23", {"start": v(10566.67, 3100) * mm, "end": v(10566.67, 4300) * mm});
            skLineSegment(sketch, "E53.0.2.24", {"start": v(3566.67, 3100) * mm, "end": v(2366.67, 3100) * mm});
            skLineSegment(sketch, "E53.0.2.25", {"start": v(25966.67, 4300) * mm, "end": v(24766.67, 4300) * mm});
            skLineSegment(sketch, "E53.0.2.26", {"start": v(22466.67, 4300) * mm, "end": v(21266.67, 4300) * mm});
            skLineSegment(sketch, "E53.0.2.27", {"start": v(15466.67, 3100) * mm, "end": v(15466.67, 4300) * mm});
            skLineSegment(sketch, "E53.0.2.28", {"start": v(18966.67, 3100) * mm, "end": v(17766.67, 3100) * mm});
            skLineSegment(sketch, "E53.0.2.29", {"start": v(24566.67, 3100) * mm, "end": v(24566.67, 4300) * mm});
            skLineSegment(sketch, "E53.0.2.30", {"start": v(24766.67, 3100) * mm, "end": v(24766.67, 4300) * mm});
            skLineSegment(sketch, "E53.0.2.31", {"start": v(5866.67, 3100) * mm, "end": v(5866.67, 4300) * mm});
            skLineSegment(sketch, "E53.0.2.32", {"start": v(18966.67, 4300) * mm, "end": v(17766.67, 4300) * mm});
            skLineSegment(sketch, "E53.0.2.33", {"start": v(8466.67, 4300) * mm, "end": v(7266.67, 4300) * mm});
            skLineSegment(sketch, "E53.0.2.34", {"start": v(11966.67, 3100) * mm, "end": v(10766.67, 3100) * mm});
            skLineSegment(sketch, "E53.0.2.35", {"start": v(3566.67, 4300) * mm, "end": v(2366.67, 4300) * mm});
            skLineSegment(sketch, "E53.0.2.36", {"start": v(10766.67, 3100) * mm, "end": v(10766.67, 4300) * mm});
            skLineSegment(sketch, "E53.0.2.37", {"start": v(4966.67, 3100) * mm, "end": v(4966.67, 4300) * mm});
            skLineSegment(sketch, "E53.0.2.38", {"start": v(3766.67, 3100) * mm, "end": v(3766.67, 4300) * mm});
            skLineSegment(sketch, "E53.0.2.39", {"start": v(17766.67, 3100) * mm, "end": v(17766.67, 4300) * mm});
            skLineSegment(sketch, "E53.0.2.40", {"start": v(17566.67, 4300) * mm, "end": v(16366.67, 4300) * mm});
            skLineSegment(sketch, "E53.0.2.41", {"start": v(4966.67, 4300) * mm, "end": v(3766.67, 4300) * mm});
            skLineSegment(sketch, "E53.0.2.42", {"start": v(23366.67, 3100) * mm, "end": v(19866.67, 3100) * mm, "construction": true});
            skLineSegment(sketch, "E53.0.2.43", {"start": v(15466.67, 4300) * mm, "end": v(14266.67, 4300) * mm});
            skLineSegment(sketch, "E53.0.2.44", {"start": v(17566.67, 3100) * mm, "end": v(17566.67, 4300) * mm});
            skLineSegment(sketch, "E53.0.2.45", {"start": v(4966.67, 3100) * mm, "end": v(3766.67, 3100) * mm});
            skLineSegment(sketch, "E53.0.2.46", {"start": v(8466.67, 3100) * mm, "end": v(7266.67, 3100) * mm});
            skLineSegment(sketch, "E53.0.2.47", {"start": v(11966.67, 4300) * mm, "end": v(10766.67, 4300) * mm});
            skLineSegment(sketch, "E53.0.2.48", {"start": v(14266.67, 3100) * mm, "end": v(14266.67, 4300) * mm});
            skLineSegment(sketch, "E53.0.2.49", {"start": v(21266.67, 3100) * mm, "end": v(21266.67, 4300) * mm});
            skLineSegment(sketch, "E53.0.2.50", {"start": v(7066.67, 3100) * mm, "end": v(7066.67, 4300) * mm});
            skLineSegment(sketch, "E53.0.2.51", {"start": v(7066.67, 3100) * mm, "end": v(5866.67, 3100) * mm});
            skLineSegment(sketch, "E53.0.2.52", {"start": v(12866.67, 3100) * mm, "end": v(12866.67, 4300) * mm});
            skLineSegment(sketch, "E53.0.2.53", {"start": v(19866.67, 3100) * mm, "end": v(19866.67, 4300) * mm});
            skLineSegment(sketch, "E53.0.2.54", {"start": v(7266.67, 3100) * mm, "end": v(7266.67, 4300) * mm});
            skLineSegment(sketch, "E53.0.2.55", {"start": v(22466.67, 3100) * mm, "end": v(21266.67, 3100) * mm});
            skLineSegment(sketch, "E53.0.2.56", {"start": v(21066.67, 3100) * mm, "end": v(19866.67, 3100) * mm});
            skLineSegment(sketch, "E53.0.3.0", {"start": v(18966.67, 4400) * mm, "end": v(18966.67, 5600) * mm});
            skLineSegment(sketch, "E53.0.3.1", {"start": v(23366.67, 4400) * mm, "end": v(23366.67, 5600) * mm});
            skLineSegment(sketch, "E53.0.3.2", {"start": v(24566.67, 5600) * mm, "end": v(23366.67, 5600) * mm});
            skLineSegment(sketch, "E53.0.3.3", {"start": v(15466.67, 4400) * mm, "end": v(14266.67, 4400) * mm});
            skLineSegment(sketch, "E53.0.3.4", {"start": v(2366.67, 4400) * mm, "end": v(2366.67, 5600) * mm});
            skLineSegment(sketch, "E53.0.3.5", {"start": v(24566.67, 4400) * mm, "end": v(23366.67, 4400) * mm});
            skLineSegment(sketch, "E53.0.3.6", {"start": v(14066.67, 4400) * mm, "end": v(12866.67, 4400) * mm});
            skLineSegment(sketch, "E53.0.3.7", {"start": v(10566.67, 4400) * mm, "end": v(9366.67, 4400) * mm});
            skLineSegment(sketch, "E53.0.3.8", {"start": v(11966.67, 4400) * mm, "end": v(11966.67, 5600) * mm});
            skLineSegment(sketch, "E53.0.3.9", {"start": v(25966.67, 4400) * mm, "end": v(25966.67, 5600) * mm});
            skLineSegment(sketch, "E53.0.3.10", {"start": v(7066.67, 5600) * mm, "end": v(5866.67, 5600) * mm});
            skLineSegment(sketch, "E53.0.3.11", {"start": v(17566.67, 4400) * mm, "end": v(16366.67, 4400) * mm});
            skLineSegment(sketch, "E53.0.3.12", {"start": v(10566.67, 5600) * mm, "end": v(9366.67, 5600) * mm});
            skLineSegment(sketch, "E53.0.3.13", {"start": v(25966.67, 4400) * mm, "end": v(24766.67, 4400) * mm});
            skLineSegment(sketch, "E53.0.3.14", {"start": v(14066.67, 4400) * mm, "end": v(14066.67, 5600) * mm});
            skLineSegment(sketch, "E53.0.3.15", {"start": v(16366.67, 4400) * mm, "end": v(16366.67, 5600) * mm});
            skLineSegment(sketch, "E53.0.3.16", {"start": v(8466.67, 4400) * mm, "end": v(8466.67, 5600) * mm});
            skLineSegment(sketch, "E53.0.3.17", {"start": v(21066.67, 4400) * mm, "end": v(21066.67, 5600) * mm});
            skLineSegment(sketch, "E53.0.3.18", {"start": v(22466.67, 4400) * mm, "end": v(22466.67, 5600) * mm});
            skLineSegment(sketch, "E53.0.3.19", {"start": v(21066.67, 5600) * mm, "end": v(19866.67, 5600) * mm});
            skLineSegment(sketch, "E53.0.3.20", {"start": v(3566.67, 4400) * mm, "end": v(3566.67, 5600) * mm});
            skLineSegment(sketch, "E53.0.3.21", {"start": v(14066.67, 5600) * mm, "end": v(12866.67, 5600) * mm});
            skLineSegment(sketch, "E53.0.3.22", {"start": v(9366.67, 4400) * mm, "end": v(9366.67, 5600) * mm});
            skLineSegment(sketch, "E53.0.3.23", {"start": v(10566.67, 4400) * mm, "end": v(10566.67, 5600) * mm});
            skLineSegment(sketch, "E53.0.3.24", {"start": v(3566.67, 4400) * mm, "end": v(2366.67, 4400) * mm});
            skLineSegment(sketch, "E53.0.3.25", {"start": v(25966.67, 5600) * mm, "end": v(24766.67, 5600) * mm});
            skLineSegment(sketch, "E53.0.3.26", {"start": v(22466.67, 5600) * mm, "end": v(21266.67, 5600) * mm});
            skLineSegment(sketch, "E53.0.3.27", {"start": v(15466.67, 4400) * mm, "end": v(15466.67, 5600) * mm});
            skLineSegment(sketch, "E53.0.3.28", {"start": v(18966.67, 4400) * mm, "end": v(17766.67, 4400) * mm});
            skLineSegment(sketch, "E53.0.3.29", {"start": v(24566.67, 4400) * mm, "end": v(24566.67, 5600) * mm});
            skLineSegment(sketch, "E53.0.3.30", {"start": v(24766.67, 4400) * mm, "end": v(24766.67, 5600) * mm});
            skLineSegment(sketch, "E53.0.3.31", {"start": v(5866.67, 4400) * mm, "end": v(5866.67, 5600) * mm});
            skLineSegment(sketch, "E53.0.3.32", {"start": v(18966.67, 5600) * mm, "end": v(17766.67, 5600) * mm});
            skLineSegment(sketch, "E53.0.3.33", {"start": v(8466.67, 5600) * mm, "end": v(7266.67, 5600) * mm});
            skLineSegment(sketch, "E53.0.3.34", {"start": v(11966.67, 4400) * mm, "end": v(10766.67, 4400) * mm});
            skLineSegment(sketch, "E53.0.3.35", {"start": v(3566.67, 5600) * mm, "end": v(2366.67, 5600) * mm});
            skLineSegment(sketch, "E53.0.3.36", {"start": v(10766.67, 4400) * mm, "end": v(10766.67, 5600) * mm});
            skLineSegment(sketch, "E53.0.3.37", {"start": v(4966.67, 4400) * mm, "end": v(4966.67, 5600) * mm});
            skLineSegment(sketch, "E53.0.3.38", {"start": v(3766.67, 4400) * mm, "end": v(3766.67, 5600) * mm});
            skLineSegment(sketch, "E53.0.3.39", {"start": v(17766.67, 4400) * mm, "end": v(17766.67, 5600) * mm});
            skLineSegment(sketch, "E53.0.3.40", {"start": v(17566.67, 5600) * mm, "end": v(16366.67, 5600) * mm});
            skLineSegment(sketch, "E53.0.3.41", {"start": v(4966.67, 5600) * mm, "end": v(3766.67, 5600) * mm});
            skLineSegment(sketch, "E53.0.3.42", {"start": v(23366.67, 4400) * mm, "end": v(19866.67, 4400) * mm, "construction": true});
            skLineSegment(sketch, "E53.0.3.43", {"start": v(15466.67, 5600) * mm, "end": v(14266.67, 5600) * mm});
            skLineSegment(sketch, "E53.0.3.44", {"start": v(17566.67, 4400) * mm, "end": v(17566.67, 5600) * mm});
            skLineSegment(sketch, "E53.0.3.45", {"start": v(4966.67, 4400) * mm, "end": v(3766.67, 4400) * mm});
            skLineSegment(sketch, "E53.0.3.46", {"start": v(8466.67, 4400) * mm, "end": v(7266.67, 4400) * mm});
            skLineSegment(sketch, "E53.0.3.47", {"start": v(11966.67, 5600) * mm, "end": v(10766.67, 5600) * mm});
            skLineSegment(sketch, "E53.0.3.48", {"start": v(14266.67, 4400) * mm, "end": v(14266.67, 5600) * mm});
            skLineSegment(sketch, "E53.0.3.49", {"start": v(21266.67, 4400) * mm, "end": v(21266.67, 5600) * mm});
            skLineSegment(sketch, "E53.0.3.50", {"start": v(7066.67, 4400) * mm, "end": v(7066.67, 5600) * mm});
            skLineSegment(sketch, "E53.0.3.51", {"start": v(7066.67, 4400) * mm, "end": v(5866.67, 4400) * mm});
            skLineSegment(sketch, "E53.0.3.52", {"start": v(12866.67, 4400) * mm, "end": v(12866.67, 5600) * mm});
            skLineSegment(sketch, "E53.0.3.53", {"start": v(19866.67, 4400) * mm, "end": v(19866.67, 5600) * mm});
            skLineSegment(sketch, "E53.0.3.54", {"start": v(7266.67, 4400) * mm, "end": v(7266.67, 5600) * mm});
            skLineSegment(sketch, "E53.0.3.55", {"start": v(22466.67, 4400) * mm, "end": v(21266.67, 4400) * mm});
            skLineSegment(sketch, "E53.0.3.56", {"start": v(21066.67, 4400) * mm, "end": v(19866.67, 4400) * mm});
            skLineSegment(sketch, "E53.0.4.0", {"start": v(18966.67, 5700) * mm, "end": v(18966.67, 6900) * mm});
            skLineSegment(sketch, "E53.0.4.1", {"start": v(23366.67, 5700) * mm, "end": v(23366.67, 6900) * mm});
            skLineSegment(sketch, "E53.0.4.2", {"start": v(24566.67, 6900) * mm, "end": v(23366.67, 6900) * mm});
            skLineSegment(sketch, "E53.0.4.3", {"start": v(15466.67, 5700) * mm, "end": v(14266.67, 5700) * mm});
            skLineSegment(sketch, "E53.0.4.4", {"start": v(2366.67, 5700) * mm, "end": v(2366.67, 6900) * mm});
            skLineSegment(sketch, "E53.0.4.5", {"start": v(24566.67, 5700) * mm, "end": v(23366.67, 5700) * mm});
            skLineSegment(sketch, "E53.0.4.6", {"start": v(14066.67, 5700) * mm, "end": v(12866.67, 5700) * mm});
            skLineSegment(sketch, "E53.0.4.7", {"start": v(10566.67, 5700) * mm, "end": v(9366.67, 5700) * mm});
            skLineSegment(sketch, "E53.0.4.8", {"start": v(11966.67, 5700) * mm, "end": v(11966.67, 6900) * mm});
            skLineSegment(sketch, "E53.0.4.9", {"start": v(25966.67, 5700) * mm, "end": v(25966.67, 6900) * mm});
            skLineSegment(sketch, "E53.0.4.10", {"start": v(7066.67, 6900) * mm, "end": v(5866.67, 6900) * mm});
            skLineSegment(sketch, "E53.0.4.11", {"start": v(17566.67, 5700) * mm, "end": v(16366.67, 5700) * mm});
            skLineSegment(sketch, "E53.0.4.12", {"start": v(10566.67, 6900) * mm, "end": v(9366.67, 6900) * mm});
            skLineSegment(sketch, "E53.0.4.13", {"start": v(25966.67, 5700) * mm, "end": v(24766.67, 5700) * mm});
            skLineSegment(sketch, "E53.0.4.14", {"start": v(14066.67, 5700) * mm, "end": v(14066.67, 6900) * mm});
            skLineSegment(sketch, "E53.0.4.15", {"start": v(16366.67, 5700) * mm, "end": v(16366.67, 6900) * mm});
            skLineSegment(sketch, "E53.0.4.16", {"start": v(8466.67, 5700) * mm, "end": v(8466.67, 6900) * mm});
            skLineSegment(sketch, "E53.0.4.17", {"start": v(21066.67, 5700) * mm, "end": v(21066.67, 6900) * mm});
            skLineSegment(sketch, "E53.0.4.18", {"start": v(22466.67, 5700) * mm, "end": v(22466.67, 6900) * mm});
            skLineSegment(sketch, "E53.0.4.19", {"start": v(21066.67, 6900) * mm, "end": v(19866.67, 6900) * mm});
            skLineSegment(sketch, "E53.0.4.20", {"start": v(3566.67, 5700) * mm, "end": v(3566.67, 6900) * mm});
            skLineSegment(sketch, "E53.0.4.21", {"start": v(14066.67, 6900) * mm, "end": v(12866.67, 6900) * mm});
            skLineSegment(sketch, "E53.0.4.22", {"start": v(9366.67, 5700) * mm, "end": v(9366.67, 6900) * mm});
            skLineSegment(sketch, "E53.0.4.23", {"start": v(10566.67, 5700) * mm, "end": v(10566.67, 6900) * mm});
            skLineSegment(sketch, "E53.0.4.24", {"start": v(3566.67, 5700) * mm, "end": v(2366.67, 5700) * mm});
            skLineSegment(sketch, "E53.0.4.25", {"start": v(25966.67, 6900) * mm, "end": v(24766.67, 6900) * mm});
            skLineSegment(sketch, "E53.0.4.26", {"start": v(22466.67, 6900) * mm, "end": v(21266.67, 6900) * mm});
            skLineSegment(sketch, "E53.0.4.27", {"start": v(15466.67, 5700) * mm, "end": v(15466.67, 6900) * mm});
            skLineSegment(sketch, "E53.0.4.28", {"start": v(18966.67, 5700) * mm, "end": v(17766.67, 5700) * mm});
            skLineSegment(sketch, "E53.0.4.29", {"start": v(24566.67, 5700) * mm, "end": v(24566.67, 6900) * mm});
            skLineSegment(sketch, "E53.0.4.30", {"start": v(24766.67, 5700) * mm, "end": v(24766.67, 6900) * mm});
            skLineSegment(sketch, "E53.0.4.31", {"start": v(5866.67, 5700) * mm, "end": v(5866.67, 6900) * mm});
            skLineSegment(sketch, "E53.0.4.32", {"start": v(18966.67, 6900) * mm, "end": v(17766.67, 6900) * mm});
            skLineSegment(sketch, "E53.0.4.33", {"start": v(8466.67, 6900) * mm, "end": v(7266.67, 6900) * mm});
            skLineSegment(sketch, "E53.0.4.34", {"start": v(11966.67, 5700) * mm, "end": v(10766.67, 5700) * mm});
            skLineSegment(sketch, "E53.0.4.35", {"start": v(3566.67, 6900) * mm, "end": v(2366.67, 6900) * mm});
            skLineSegment(sketch, "E53.0.4.36", {"start": v(10766.67, 5700) * mm, "end": v(10766.67, 6900) * mm});
            skLineSegment(sketch, "E53.0.4.37", {"start": v(4966.67, 5700) * mm, "end": v(4966.67, 6900) * mm});
            skLineSegment(sketch, "E53.0.4.38", {"start": v(3766.67, 5700) * mm, "end": v(3766.67, 6900) * mm});
            skLineSegment(sketch, "E53.0.4.39", {"start": v(17766.67, 5700) * mm, "end": v(17766.67, 6900) * mm});
            skLineSegment(sketch, "E53.0.4.40", {"start": v(17566.67, 6900) * mm, "end": v(16366.67, 6900) * mm});
            skLineSegment(sketch, "E53.0.4.41", {"start": v(4966.67, 6900) * mm, "end": v(3766.67, 6900) * mm});
            skLineSegment(sketch, "E53.0.4.42", {"start": v(23366.67, 5700) * mm, "end": v(19866.67, 5700) * mm, "construction": true});
            skLineSegment(sketch, "E53.0.4.43", {"start": v(15466.67, 6900) * mm, "end": v(14266.67, 6900) * mm});
            skLineSegment(sketch, "E53.0.4.44", {"start": v(17566.67, 5700) * mm, "end": v(17566.67, 6900) * mm});
            skLineSegment(sketch, "E53.0.4.45", {"start": v(4966.67, 5700) * mm, "end": v(3766.67, 5700) * mm});
            skLineSegment(sketch, "E53.0.4.46", {"start": v(8466.67, 5700) * mm, "end": v(7266.67, 5700) * mm});
            skLineSegment(sketch, "E53.0.4.47", {"start": v(11966.67, 6900) * mm, "end": v(10766.67, 6900) * mm});
            skLineSegment(sketch, "E53.0.4.48", {"start": v(14266.67, 5700) * mm, "end": v(14266.67, 6900) * mm});
            skLineSegment(sketch, "E53.0.4.49", {"start": v(21266.67, 5700) * mm, "end": v(21266.67, 6900) * mm});
            skLineSegment(sketch, "E53.0.4.50", {"start": v(7066.67, 5700) * mm, "end": v(7066.67, 6900) * mm});
            skLineSegment(sketch, "E53.0.4.51", {"start": v(7066.67, 5700) * mm, "end": v(5866.67, 5700) * mm});
            skLineSegment(sketch, "E53.0.4.52", {"start": v(12866.67, 5700) * mm, "end": v(12866.67, 6900) * mm});
            skLineSegment(sketch, "E53.0.4.53", {"start": v(19866.67, 5700) * mm, "end": v(19866.67, 6900) * mm});
            skLineSegment(sketch, "E53.0.4.54", {"start": v(7266.67, 5700) * mm, "end": v(7266.67, 6900) * mm});
            skLineSegment(sketch, "E53.0.4.55", {"start": v(22466.67, 5700) * mm, "end": v(21266.67, 5700) * mm});
            skLineSegment(sketch, "E53.0.4.56", {"start": v(21066.67, 5700) * mm, "end": v(19866.67, 5700) * mm});
            skLineSegment(sketch, "E53.0.5.0", {"start": v(18966.67, 7000) * mm, "end": v(18966.67, 8200) * mm});
            skLineSegment(sketch, "E53.0.5.1", {"start": v(23366.67, 7000) * mm, "end": v(23366.67, 8200) * mm});
            skLineSegment(sketch, "E53.0.5.2", {"start": v(24566.67, 8200) * mm, "end": v(23366.67, 8200) * mm});
            skLineSegment(sketch, "E53.0.5.3", {"start": v(15466.67, 7000) * mm, "end": v(14266.67, 7000) * mm});
            skLineSegment(sketch, "E53.0.5.4", {"start": v(2366.67, 7000) * mm, "end": v(2366.67, 8200) * mm});
            skLineSegment(sketch, "E53.0.5.5", {"start": v(24566.67, 7000) * mm, "end": v(23366.67, 7000) * mm});
            skLineSegment(sketch, "E53.0.5.6", {"start": v(14066.67, 7000) * mm, "end": v(12866.67, 7000) * mm});
            skLineSegment(sketch, "E53.0.5.7", {"start": v(10566.67, 7000) * mm, "end": v(9366.67, 7000) * mm});
            skLineSegment(sketch, "E53.0.5.8", {"start": v(11966.67, 7000) * mm, "end": v(11966.67, 8200) * mm});
            skLineSegment(sketch, "E53.0.5.9", {"start": v(25966.67, 7000) * mm, "end": v(25966.67, 8200) * mm});
            skLineSegment(sketch, "E53.0.5.10", {"start": v(7066.67, 8200) * mm, "end": v(5866.67, 8200) * mm});
            skLineSegment(sketch, "E53.0.5.11", {"start": v(17566.67, 7000) * mm, "end": v(16366.67, 7000) * mm});
            skLineSegment(sketch, "E53.0.5.12", {"start": v(10566.67, 8200) * mm, "end": v(9366.67, 8200) * mm});
            skLineSegment(sketch, "E53.0.5.13", {"start": v(25966.67, 7000) * mm, "end": v(24766.67, 7000) * mm});
            skLineSegment(sketch, "E53.0.5.14", {"start": v(14066.67, 7000) * mm, "end": v(14066.67, 8200) * mm});
            skLineSegment(sketch, "E53.0.5.15", {"start": v(16366.67, 7000) * mm, "end": v(16366.67, 8200) * mm});
            skLineSegment(sketch, "E53.0.5.16", {"start": v(8466.67, 7000) * mm, "end": v(8466.67, 8200) * mm});
            skLineSegment(sketch, "E53.0.5.17", {"start": v(21066.67, 7000) * mm, "end": v(21066.67, 8200) * mm});
            skLineSegment(sketch, "E53.0.5.18", {"start": v(22466.67, 7000) * mm, "end": v(22466.67, 8200) * mm});
            skLineSegment(sketch, "E53.0.5.19", {"start": v(21066.67, 8200) * mm, "end": v(19866.67, 8200) * mm});
            skLineSegment(sketch, "E53.0.5.20", {"start": v(3566.67, 7000) * mm, "end": v(3566.67, 8200) * mm});
            skLineSegment(sketch, "E53.0.5.21", {"start": v(14066.67, 8200) * mm, "end": v(12866.67, 8200) * mm});
            skLineSegment(sketch, "E53.0.5.22", {"start": v(9366.67, 7000) * mm, "end": v(9366.67, 8200) * mm});
            skLineSegment(sketch, "E53.0.5.23", {"start": v(10566.67, 7000) * mm, "end": v(10566.67, 8200) * mm});
            skLineSegment(sketch, "E53.0.5.24", {"start": v(3566.67, 7000) * mm, "end": v(2366.67, 7000) * mm});
            skLineSegment(sketch, "E53.0.5.25", {"start": v(25966.67, 8200) * mm, "end": v(24766.67, 8200) * mm});
            skLineSegment(sketch, "E53.0.5.26", {"start": v(22466.67, 8200) * mm, "end": v(21266.67, 8200) * mm});
            skLineSegment(sketch, "E53.0.5.27", {"start": v(15466.67, 7000) * mm, "end": v(15466.67, 8200) * mm});
            skLineSegment(sketch, "E53.0.5.28", {"start": v(18966.67, 7000) * mm, "end": v(17766.67, 7000) * mm});
            skLineSegment(sketch, "E53.0.5.29", {"start": v(24566.67, 7000) * mm, "end": v(24566.67, 8200) * mm});
            skLineSegment(sketch, "E53.0.5.30", {"start": v(24766.67, 7000) * mm, "end": v(24766.67, 8200) * mm});
            skLineSegment(sketch, "E53.0.5.31", {"start": v(5866.67, 7000) * mm, "end": v(5866.67, 8200) * mm});
            skLineSegment(sketch, "E53.0.5.32", {"start": v(18966.67, 8200) * mm, "end": v(17766.67, 8200) * mm});
            skLineSegment(sketch, "E53.0.5.33", {"start": v(8466.67, 8200) * mm, "end": v(7266.67, 8200) * mm});
            skLineSegment(sketch, "E53.0.5.34", {"start": v(11966.67, 7000) * mm, "end": v(10766.67, 7000) * mm});
            skLineSegment(sketch, "E53.0.5.35", {"start": v(3566.67, 8200) * mm, "end": v(2366.67, 8200) * mm});
            skLineSegment(sketch, "E53.0.5.36", {"start": v(10766.67, 7000) * mm, "end": v(10766.67, 8200) * mm});
            skLineSegment(sketch, "E53.0.5.37", {"start": v(4966.67, 7000) * mm, "end": v(4966.67, 8200) * mm});
            skLineSegment(sketch, "E53.0.5.38", {"start": v(3766.67, 7000) * mm, "end": v(3766.67, 8200) * mm});
            skLineSegment(sketch, "E53.0.5.39", {"start": v(17766.67, 7000) * mm, "end": v(17766.67, 8200) * mm});
            skLineSegment(sketch, "E53.0.5.40", {"start": v(17566.67, 8200) * mm, "end": v(16366.67, 8200) * mm});
            skLineSegment(sketch, "E53.0.5.41", {"start": v(4966.67, 8200) * mm, "end": v(3766.67, 8200) * mm});
            skLineSegment(sketch, "E53.0.5.42", {"start": v(23366.67, 7000) * mm, "end": v(19866.67, 7000) * mm, "construction": true});
            skLineSegment(sketch, "E53.0.5.43", {"start": v(15466.67, 8200) * mm, "end": v(14266.67, 8200) * mm});
            skLineSegment(sketch, "E53.0.5.44", {"start": v(17566.67, 7000) * mm, "end": v(17566.67, 8200) * mm});
            skLineSegment(sketch, "E53.0.5.45", {"start": v(4966.67, 7000) * mm, "end": v(3766.67, 7000) * mm});
            skLineSegment(sketch, "E53.0.5.46", {"start": v(8466.67, 7000) * mm, "end": v(7266.67, 7000) * mm});
            skLineSegment(sketch, "E53.0.5.47", {"start": v(11966.67, 8200) * mm, "end": v(10766.67, 8200) * mm});
            skLineSegment(sketch, "E53.0.5.48", {"start": v(14266.67, 7000) * mm, "end": v(14266.67, 8200) * mm});
            skLineSegment(sketch, "E53.0.5.49", {"start": v(21266.67, 7000) * mm, "end": v(21266.67, 8200) * mm});
            skLineSegment(sketch, "E53.0.5.50", {"start": v(7066.67, 7000) * mm, "end": v(7066.67, 8200) * mm});
            skLineSegment(sketch, "E53.0.5.51", {"start": v(7066.67, 7000) * mm, "end": v(5866.67, 7000) * mm});
            skLineSegment(sketch, "E53.0.5.52", {"start": v(12866.67, 7000) * mm, "end": v(12866.67, 8200) * mm});
            skLineSegment(sketch, "E53.0.5.53", {"start": v(19866.67, 7000) * mm, "end": v(19866.67, 8200) * mm});
            skLineSegment(sketch, "E53.0.5.54", {"start": v(7266.67, 7000) * mm, "end": v(7266.67, 8200) * mm});
            skLineSegment(sketch, "E53.0.5.55", {"start": v(22466.67, 7000) * mm, "end": v(21266.67, 7000) * mm});
            skLineSegment(sketch, "E53.0.5.56", {"start": v(21066.67, 7000) * mm, "end": v(19866.67, 7000) * mm});
            skLineSegment(sketch, "E53.0.6.0", {"start": v(18966.67, 8300) * mm, "end": v(18966.67, 9500) * mm});
            skLineSegment(sketch, "E53.0.6.1", {"start": v(23366.67, 8300) * mm, "end": v(23366.67, 9500) * mm});
            skLineSegment(sketch, "E53.0.6.2", {"start": v(24566.67, 9500) * mm, "end": v(23366.67, 9500) * mm});
            skLineSegment(sketch, "E53.0.6.3", {"start": v(15466.67, 8300) * mm, "end": v(14266.67, 8300) * mm});
            skLineSegment(sketch, "E53.0.6.4", {"start": v(2366.67, 8300) * mm, "end": v(2366.67, 9500) * mm});
            skLineSegment(sketch, "E53.0.6.5", {"start": v(24566.67, 8300) * mm, "end": v(23366.67, 8300) * mm});
            skLineSegment(sketch, "E53.0.6.6", {"start": v(14066.67, 8300) * mm, "end": v(12866.67, 8300) * mm});
            skLineSegment(sketch, "E53.0.6.7", {"start": v(10566.67, 8300) * mm, "end": v(9366.67, 8300) * mm});
            skLineSegment(sketch, "E53.0.6.8", {"start": v(11966.67, 8300) * mm, "end": v(11966.67, 9500) * mm});
            skLineSegment(sketch, "E53.0.6.9", {"start": v(25966.67, 8300) * mm, "end": v(25966.67, 9500) * mm});
            skLineSegment(sketch, "E53.0.6.10", {"start": v(7066.67, 9500) * mm, "end": v(5866.67, 9500) * mm});
            skLineSegment(sketch, "E53.0.6.11", {"start": v(17566.67, 8300) * mm, "end": v(16366.67, 8300) * mm});
            skLineSegment(sketch, "E53.0.6.12", {"start": v(10566.67, 9500) * mm, "end": v(9366.67, 9500) * mm});
            skLineSegment(sketch, "E53.0.6.13", {"start": v(25966.67, 8300) * mm, "end": v(24766.67, 8300) * mm});
            skLineSegment(sketch, "E53.0.6.14", {"start": v(14066.67, 8300) * mm, "end": v(14066.67, 9500) * mm});
            skLineSegment(sketch, "E53.0.6.15", {"start": v(16366.67, 8300) * mm, "end": v(16366.67, 9500) * mm});
            skLineSegment(sketch, "E53.0.6.16", {"start": v(8466.67, 8300) * mm, "end": v(8466.67, 9500) * mm});
            skLineSegment(sketch, "E53.0.6.17", {"start": v(21066.67, 8300) * mm, "end": v(21066.67, 9500) * mm});
            skLineSegment(sketch, "E53.0.6.18", {"start": v(22466.67, 8300) * mm, "end": v(22466.67, 9500) * mm});
            skLineSegment(sketch, "E53.0.6.19", {"start": v(21066.67, 9500) * mm, "end": v(19866.67, 9500) * mm});
            skLineSegment(sketch, "E53.0.6.20", {"start": v(3566.67, 8300) * mm, "end": v(3566.67, 9500) * mm});
            skLineSegment(sketch, "E53.0.6.21", {"start": v(14066.67, 9500) * mm, "end": v(12866.67, 9500) * mm});
            skLineSegment(sketch, "E53.0.6.22", {"start": v(9366.67, 8300) * mm, "end": v(9366.67, 9500) * mm});
            skLineSegment(sketch, "E53.0.6.23", {"start": v(10566.67, 8300) * mm, "end": v(10566.67, 9500) * mm});
            skLineSegment(sketch, "E53.0.6.24", {"start": v(3566.67, 8300) * mm, "end": v(2366.67, 8300) * mm});
            skLineSegment(sketch, "E53.0.6.25", {"start": v(25966.67, 9500) * mm, "end": v(24766.67, 9500) * mm});
            skLineSegment(sketch, "E53.0.6.26", {"start": v(22466.67, 9500) * mm, "end": v(21266.67, 9500) * mm});
            skLineSegment(sketch, "E53.0.6.27", {"start": v(15466.67, 8300) * mm, "end": v(15466.67, 9500) * mm});
            skLineSegment(sketch, "E53.0.6.28", {"start": v(18966.67, 8300) * mm, "end": v(17766.67, 8300) * mm});
            skLineSegment(sketch, "E53.0.6.29", {"start": v(24566.67, 8300) * mm, "end": v(24566.67, 9500) * mm});
            skLineSegment(sketch, "E53.0.6.30", {"start": v(24766.67, 8300) * mm, "end": v(24766.67, 9500) * mm});
            skLineSegment(sketch, "E53.0.6.31", {"start": v(5866.67, 8300) * mm, "end": v(5866.67, 9500) * mm});
            skLineSegment(sketch, "E53.0.6.32", {"start": v(18966.67, 9500) * mm, "end": v(17766.67, 9500) * mm});
            skLineSegment(sketch, "E53.0.6.33", {"start": v(8466.67, 9500) * mm, "end": v(7266.67, 9500) * mm});
            skLineSegment(sketch, "E53.0.6.34", {"start": v(11966.67, 8300) * mm, "end": v(10766.67, 8300) * mm});
            skLineSegment(sketch, "E53.0.6.35", {"start": v(3566.67, 9500) * mm, "end": v(2366.67, 9500) * mm});
            skLineSegment(sketch, "E53.0.6.36", {"start": v(10766.67, 8300) * mm, "end": v(10766.67, 9500) * mm});
            skLineSegment(sketch, "E53.0.6.37", {"start": v(4966.67, 8300) * mm, "end": v(4966.67, 9500) * mm});
            skLineSegment(sketch, "E53.0.6.38", {"start": v(3766.67, 8300) * mm, "end": v(3766.67, 9500) * mm});
            skLineSegment(sketch, "E53.0.6.39", {"start": v(17766.67, 8300) * mm, "end": v(17766.67, 9500) * mm});
            skLineSegment(sketch, "E53.0.6.40", {"start": v(17566.67, 9500) * mm, "end": v(16366.67, 9500) * mm});
            skLineSegment(sketch, "E53.0.6.41", {"start": v(4966.67, 9500) * mm, "end": v(3766.67, 9500) * mm});
            skLineSegment(sketch, "E53.0.6.42", {"start": v(23366.67, 8300) * mm, "end": v(19866.67, 8300) * mm, "construction": true});
            skLineSegment(sketch, "E53.0.6.43", {"start": v(15466.67, 9500) * mm, "end": v(14266.67, 9500) * mm});
            skLineSegment(sketch, "E53.0.6.44", {"start": v(17566.67, 8300) * mm, "end": v(17566.67, 9500) * mm});
            skLineSegment(sketch, "E53.0.6.45", {"start": v(4966.67, 8300) * mm, "end": v(3766.67, 8300) * mm});
            skLineSegment(sketch, "E53.0.6.46", {"start": v(8466.67, 8300) * mm, "end": v(7266.67, 8300) * mm});
            skLineSegment(sketch, "E53.0.6.47", {"start": v(11966.67, 9500) * mm, "end": v(10766.67, 9500) * mm});
            skLineSegment(sketch, "E53.0.6.48", {"start": v(14266.67, 8300) * mm, "end": v(14266.67, 9500) * mm});
            skLineSegment(sketch, "E53.0.6.49", {"start": v(21266.67, 8300) * mm, "end": v(21266.67, 9500) * mm});
            skLineSegment(sketch, "E53.0.6.50", {"start": v(7066.67, 8300) * mm, "end": v(7066.67, 9500) * mm});
            skLineSegment(sketch, "E53.0.6.51", {"start": v(7066.67, 8300) * mm, "end": v(5866.67, 8300) * mm});
            skLineSegment(sketch, "E53.0.6.52", {"start": v(12866.67, 8300) * mm, "end": v(12866.67, 9500) * mm});
            skLineSegment(sketch, "E53.0.6.53", {"start": v(19866.67, 8300) * mm, "end": v(19866.67, 9500) * mm});
            skLineSegment(sketch, "E53.0.6.54", {"start": v(7266.67, 8300) * mm, "end": v(7266.67, 9500) * mm});
            skLineSegment(sketch, "E53.0.6.55", {"start": v(22466.67, 8300) * mm, "end": v(21266.67, 8300) * mm});
            skLineSegment(sketch, "E53.0.6.56", {"start": v(21066.67, 8300) * mm, "end": v(19866.67, 8300) * mm});
            skLineSegment(sketch, "E53.direction1", {"start": v(2366.67, 500) * mm, "end": v(3666.67, 500) * mm, "construction": true});
            skLineSegment(sketch, "E53.direction2", {"start": v(2366.67, 500) * mm, "end": v(2366.67, 1800) * mm, "construction": true});
            skLineSegment(sketch, "E54.0", {"start": v(-270, 22270) * mm, "end": v(-270, -270) * mm, "construction": true});
            skLineSegment(sketch, "E55", {"start": v(-270, 11000) * mm, "end": v(31110.38, 11000) * mm, "construction": true});
            skLineSegment(sketch, "E56.MirrorCS", {"start": v(21066.67, 17600) * mm, "end": v(19866.67, 17600) * mm});
            skLineSegment(sketch, "E57.MirrorCS", {"start": v(22466.67, 21500) * mm, "end": v(21266.67, 21500) * mm});
            skLineSegment(sketch, "E58.MirrorCS", {"start": v(22466.67, 17600) * mm, "end": v(21266.67, 17600) * mm});
            skLineSegment(sketch, "E59.MirrorCS", {"start": v(21066.67, 18900) * mm, "end": v(19866.67, 18900) * mm});
            skLineSegment(sketch, "E60.MirrorCS", {"start": v(22466.67, 13700) * mm, "end": v(21266.67, 13700) * mm});
            skLineSegment(sketch, "E61.MirrorCS", {"start": v(3566.67, 21500) * mm, "end": v(2366.67, 21500) * mm});
            skLineSegment(sketch, "E62.MirrorCS", {"start": v(2366.67, 21500) * mm, "end": v(2366.67, 20300) * mm});
            skLineSegment(sketch, "E63.MirrorCS", {"start": v(21066.67, 13700) * mm, "end": v(19866.67, 13700) * mm});
            skLineSegment(sketch, "E64.MirrorCS", {"start": v(22466.67, 15000) * mm, "end": v(21266.67, 15000) * mm});
            skLineSegment(sketch, "E65.MirrorCS", {"start": v(26966.67, 20200) * mm, "end": v(26966.67, 19000) * mm});
            skLineSegment(sketch, "E66.MirrorCS", {"start": v(22466.67, 16300) * mm, "end": v(21266.67, 16300) * mm});
            skLineSegment(sketch, "E67.MirrorCS", {"start": v(24566.67, 19000) * mm, "end": v(23366.67, 19000) * mm});
            skLineSegment(sketch, "E68.MirrorCS", {"start": v(21066.67, 15000) * mm, "end": v(19866.67, 15000) * mm});
            skLineSegment(sketch, "E69.MirrorCS", {"start": v(22466.67, 20200) * mm, "end": v(21266.67, 20200) * mm});
            skLineSegment(sketch, "E70.MirrorCS", {"start": v(21066.67, 16300) * mm, "end": v(19866.67, 16300) * mm});
            skLineSegment(sketch, "E71.MirrorCS", {"start": v(21066.67, 20200) * mm, "end": v(19866.67, 20200) * mm});
            skLineSegment(sketch, "E72.MirrorCS", {"start": v(28166.67, 20300) * mm, "end": v(26966.67, 20300) * mm});
            skLineSegment(sketch, "E73.MirrorCS", {"start": v(21066.67, 21500) * mm, "end": v(19866.67, 21500) * mm});
            skLineSegment(sketch, "E74.MirrorCS", {"start": v(22466.67, 18900) * mm, "end": v(21266.67, 18900) * mm});
            skLineSegment(sketch, "E75.MirrorCS", {"start": v(10766.67, 18900) * mm, "end": v(10766.67, 17700) * mm});
            skLineSegment(sketch, "E76.MirrorCS", {"start": v(25966.67, 16400) * mm, "end": v(24766.67, 16400) * mm});
            skLineSegment(sketch, "E77.MirrorCS", {"start": v(7066.67, 15100) * mm, "end": v(5866.67, 15100) * mm});
            skLineSegment(sketch, "E78.MirrorCS", {"start": v(2366.67, 17600) * mm, "end": v(2366.67, 16400) * mm});
            skLineSegment(sketch, "E79.MirrorCS", {"start": v(7066.67, 13700) * mm, "end": v(5866.67, 13700) * mm});
            skLineSegment(sketch, "E80.MirrorCS", {"start": v(19866.67, 18900) * mm, "end": v(19866.67, 17700) * mm});
            skLineSegment(sketch, "E81.MirrorCS", {"start": v(11966.67, 21500) * mm, "end": v(11966.67, 20300) * mm});
            skLineSegment(sketch, "E82.MirrorCS", {"start": v(19866.67, 15000) * mm, "end": v(19866.67, 13800) * mm});
            skLineSegment(sketch, "E83.MirrorCS", {"start": v(26966.67, 20300) * mm, "end": v(27932.88, 20300) * mm, "construction": true});
            skLineSegment(sketch, "E84.MirrorCS", {"start": v(11966.67, 16300) * mm, "end": v(10766.67, 16300) * mm});
            skLineSegment(sketch, "E85.MirrorCS", {"start": v(25966.67, 19000) * mm, "end": v(24766.67, 19000) * mm});
            skLineSegment(sketch, "E86.MirrorCS", {"start": v(15466.67, 15000) * mm, "end": v(15466.67, 13800) * mm});
            skLineSegment(sketch, "E87.MirrorCS", {"start": v(26966.67, 17600) * mm, "end": v(26966.67, 16400) * mm});
            skLineSegment(sketch, "E88.MirrorCS", {"start": v(17566.67, 16300) * mm, "end": v(16366.67, 16300) * mm});
            skLineSegment(sketch, "E89.MirrorCS", {"start": v(17566.67, 16300) * mm, "end": v(17566.67, 15100) * mm});
            skLineSegment(sketch, "E90.MirrorCS", {"start": v(19866.67, 21500) * mm, "end": v(19866.67, 20300) * mm});
            skLineSegment(sketch, "E91.MirrorCS", {"start": v(2366.67, 21500) * mm, "end": v(2366.67, 20200) * mm, "construction": true});
            skLineSegment(sketch, "E92.MirrorCS", {"start": v(17766.67, 17600) * mm, "end": v(17766.67, 16400) * mm});
            skLineSegment(sketch, "E93.MirrorCS", {"start": v(18966.67, 17600) * mm, "end": v(17766.67, 17600) * mm});
            skLineSegment(sketch, "E94.MirrorCS", {"start": v(17766.67, 20200) * mm, "end": v(17766.67, 19000) * mm});
            skLineSegment(sketch, "E95.MirrorCS", {"start": v(17566.67, 17700) * mm, "end": v(16366.67, 17700) * mm});
            skLineSegment(sketch, "E96.MirrorCS", {"start": v(7066.67, 16400) * mm, "end": v(5866.67, 16400) * mm});
            skLineSegment(sketch, "E97.MirrorCS", {"start": v(3566.67, 13700) * mm, "end": v(3566.67, 12500) * mm});
            skLineSegment(sketch, "E98.MirrorCS", {"start": v(19866.67, 13700) * mm, "end": v(19866.67, 12500) * mm});
            skLineSegment(sketch, "E99.MirrorCS", {"start": v(5866.67, 17600) * mm, "end": v(5866.67, 16400) * mm});
            skLineSegment(sketch, "E100.MirrorCS", {"start": v(3566.67, 18900) * mm, "end": v(3566.67, 17700) * mm});
            skLineSegment(sketch, "E101.MirrorCS", {"start": v(11966.67, 17700) * mm, "end": v(10766.67, 17700) * mm});
            skLineSegment(sketch, "E102.MirrorCS", {"start": v(18966.67, 12500) * mm, "end": v(17766.67, 12500) * mm});
            skLineSegment(sketch, "E103.MirrorCS", {"start": v(16366.67, 15000) * mm, "end": v(16366.67, 13800) * mm});
            skLineSegment(sketch, "E104.MirrorCS", {"start": v(8466.67, 20200) * mm, "end": v(7266.67, 20200) * mm});
            skLineSegment(sketch, "E105.MirrorCS", {"start": v(21066.67, 13700) * mm, "end": v(21066.67, 12500) * mm});
            skLineSegment(sketch, "E106.MirrorCS", {"start": v(5866.67, 21500) * mm, "end": v(5866.67, 20300) * mm});
            skLineSegment(sketch, "E107.MirrorCS", {"start": v(17566.67, 15100) * mm, "end": v(16366.67, 15100) * mm});
            skLineSegment(sketch, "E108.MirrorCS", {"start": v(21066.67, 15000) * mm, "end": v(21066.67, 13800) * mm});
            skLineSegment(sketch, "E109.MirrorCS", {"start": v(2366.67, 21500) * mm, "end": v(3666.67, 21500) * mm, "construction": true});
            skLineSegment(sketch, "E110.MirrorCS", {"start": v(14066.67, 17600) * mm, "end": v(14066.67, 16400) * mm});
            skLineSegment(sketch, "E111.MirrorCS", {"start": v(24566.67, 15000) * mm, "end": v(23366.67, 15000) * mm});
            skLineSegment(sketch, "E112.MirrorCS", {"start": v(3566.67, 15000) * mm, "end": v(3566.67, 13800) * mm});
            skLineSegment(sketch, "E113.MirrorCS", {"start": v(17566.67, 18900) * mm, "end": v(17566.67, 17700) * mm});
            skLineSegment(sketch, "E114.MirrorCS", {"start": v(18966.67, 15000) * mm, "end": v(18966.67, 13800) * mm});
            skLineSegment(sketch, "E115.MirrorCS", {"start": v(24566.67, 20200) * mm, "end": v(23366.67, 20200) * mm});
            skLineSegment(sketch, "E116.MirrorCS", {"start": v(18966.67, 19000) * mm, "end": v(17766.67, 19000) * mm});
            skLineSegment(sketch, "E117.MirrorCS", {"start": v(9366.67, 17600) * mm, "end": v(9366.67, 16400) * mm});
            skLineSegment(sketch, "E118.MirrorCS", {"start": v(21066.67, 13800) * mm, "end": v(19866.67, 13800) * mm});
            skLineSegment(sketch, "E119.MirrorCS", {"start": v(4966.67, 15100) * mm, "end": v(3766.67, 15100) * mm});
            skLineSegment(sketch, "E120.MirrorCS", {"start": v(21066.67, 20200) * mm, "end": v(21066.67, 19000) * mm});
            skLineSegment(sketch, "E121.MirrorCS", {"start": v(24566.67, 17600) * mm, "end": v(23366.67, 17600) * mm});
            skLineSegment(sketch, "E122.MirrorCS", {"start": v(3566.67, 17600) * mm, "end": v(2366.67, 17600) * mm});
            skLineSegment(sketch, "E123.MirrorCS", {"start": v(10566.67, 16300) * mm, "end": v(9366.67, 16300) * mm});
            skLineSegment(sketch, "E124.MirrorCS", {"start": v(26966.67, 18900) * mm, "end": v(26966.67, 17700) * mm});
            skLineSegment(sketch, "E125.MirrorCS", {"start": v(8466.67, 17600) * mm, "end": v(7266.67, 17600) * mm});
            skLineSegment(sketch, "E126.MirrorCS", {"start": v(7066.67, 17600) * mm, "end": v(5866.67, 17600) * mm});
            skLineSegment(sketch, "E127.MirrorCS", {"start": v(23366.67, 13700) * mm, "end": v(19866.67, 13700) * mm, "construction": true});
            skLineSegment(sketch, "E128.MirrorCS", {"start": v(19866.67, 20200) * mm, "end": v(19866.67, 19000) * mm});
            skLineSegment(sketch, "E129.MirrorCS", {"start": v(18966.67, 16300) * mm, "end": v(17766.67, 16300) * mm});
            skLineSegment(sketch, "E130.MirrorCS", {"start": v(15466.67, 15100) * mm, "end": v(14266.67, 15100) * mm});
            skLineSegment(sketch, "E131.MirrorCS", {"start": v(26966.67, 15000) * mm, "end": v(26966.67, 13800) * mm});
            skLineSegment(sketch, "E132.MirrorCS", {"start": v(7066.67, 17600) * mm, "end": v(7066.67, 16400) * mm});
            skLineSegment(sketch, "E133.MirrorCS", {"start": v(8466.67, 16400) * mm, "end": v(7266.67, 16400) * mm});
            skLineSegment(sketch, "E134.MirrorCS", {"start": v(14066.67, 15100) * mm, "end": v(12866.67, 15100) * mm});
            skLineSegment(sketch, "E135.MirrorCS", {"start": v(22466.67, 16300) * mm, "end": v(22466.67, 15100) * mm});
            skLineSegment(sketch, "E136.MirrorCS", {"start": v(3566.67, 17700) * mm, "end": v(2366.67, 17700) * mm});
            skLineSegment(sketch, "E137.MirrorCS", {"start": v(22466.67, 15100) * mm, "end": v(21266.67, 15100) * mm});
            skLineSegment(sketch, "E138.MirrorCS", {"start": v(8466.67, 16300) * mm, "end": v(7266.67, 16300) * mm});
            skLineSegment(sketch, "E139.MirrorCS", {"start": v(15466.67, 18900) * mm, "end": v(14266.67, 18900) * mm});
            skLineSegment(sketch, "E140.MirrorCS", {"start": v(12866.67, 13700) * mm, "end": v(12866.67, 12500) * mm});
            skLineSegment(sketch, "E141.MirrorCS", {"start": v(14266.67, 21500) * mm, "end": v(14266.67, 20300) * mm});
            skLineSegment(sketch, "E142.MirrorCS", {"start": v(3566.67, 16300) * mm, "end": v(3566.67, 15100) * mm});
            skLineSegment(sketch, "E143.MirrorCS", {"start": v(22466.67, 16400) * mm, "end": v(21266.67, 16400) * mm});
            skLineSegment(sketch, "E144.MirrorCS", {"start": v(7266.67, 18900) * mm, "end": v(7266.67, 17700) * mm});
            skLineSegment(sketch, "E145.MirrorCS", {"start": v(18966.67, 20200) * mm, "end": v(17766.67, 20200) * mm});
            skLineSegment(sketch, "E146.MirrorCS", {"start": v(28166.67, 21500) * mm, "end": v(28166.67, 20300) * mm});
            skLineSegment(sketch, "E147.MirrorCS", {"start": v(22466.67, 20200) * mm, "end": v(22466.67, 19000) * mm});
            skLineSegment(sketch, "E148.MirrorCS", {"start": v(26966.67, 13700) * mm, "end": v(26966.67, 12500) * mm});
            skLineSegment(sketch, "E149.MirrorCS", {"start": v(28166.67, 19000) * mm, "end": v(26966.67, 19000) * mm});
            skLineSegment(sketch, "E150.MirrorCS", {"start": v(22466.67, 13700) * mm, "end": v(22466.67, 12500) * mm});
            skLineSegment(sketch, "E151.MirrorCS", {"start": v(24766.67, 21500) * mm, "end": v(24766.67, 20300) * mm});
            skLineSegment(sketch, "E152.MirrorCS", {"start": v(24766.67, 20200) * mm, "end": v(24766.67, 19000) * mm});
            skLineSegment(sketch, "E153.MirrorCS", {"start": v(18966.67, 15100) * mm, "end": v(17766.67, 15100) * mm});
            skLineSegment(sketch, "E154.MirrorCS", {"start": v(10566.67, 13700) * mm, "end": v(9366.67, 13700) * mm});
            skLineSegment(sketch, "E155.MirrorCS", {"start": v(8466.67, 19000) * mm, "end": v(7266.67, 19000) * mm});
            skLineSegment(sketch, "E156.MirrorCS", {"start": v(4966.67, 19000) * mm, "end": v(3766.67, 19000) * mm});
            skLineSegment(sketch, "E157.MirrorCS", {"start": v(3566.67, 15000) * mm, "end": v(2366.67, 15000) * mm});
            skLineSegment(sketch, "E158.MirrorCS", {"start": v(21066.67, 16400) * mm, "end": v(19866.67, 16400) * mm});
            skLineSegment(sketch, "E159.MirrorCS", {"start": v(11966.67, 12500) * mm, "end": v(10766.67, 12500) * mm});
            skLineSegment(sketch, "E160.MirrorCS", {"start": v(15466.67, 15000) * mm, "end": v(14266.67, 15000) * mm});
            skLineSegment(sketch, "E161.MirrorCS", {"start": v(14266.67, 16300) * mm, "end": v(14266.67, 15100) * mm});
            skLineSegment(sketch, "E162.MirrorCS", {"start": v(7066.67, 15000) * mm, "end": v(5866.67, 15000) * mm});
            skLineSegment(sketch, "E163.MirrorCS", {"start": v(7066.67, 20200) * mm, "end": v(7066.67, 19000) * mm});
            skLineSegment(sketch, "E164.MirrorCS", {"start": v(12866.67, 16300) * mm, "end": v(12866.67, 15100) * mm});
            skLineSegment(sketch, "E165.MirrorCS", {"start": v(7066.67, 21500) * mm, "end": v(5866.67, 21500) * mm});
            skLineSegment(sketch, "E166.MirrorCS", {"start": v(28166.67, 15000) * mm, "end": v(26966.67, 15000) * mm});
            skLineSegment(sketch, "E167.MirrorCS", {"start": v(12866.67, 17600) * mm, "end": v(12866.67, 16400) * mm});
            skLineSegment(sketch, "E168.MirrorCS", {"start": v(7066.67, 13700) * mm, "end": v(7066.67, 12500) * mm});
            skLineSegment(sketch, "E169.MirrorCS", {"start": v(12866.67, 20200) * mm, "end": v(12866.67, 19000) * mm});
            skLineSegment(sketch, "E170.MirrorCS", {"start": v(25966.67, 17600) * mm, "end": v(24766.67, 17600) * mm});
            skLineSegment(sketch, "E171.MirrorCS", {"start": v(3566.67, 12500) * mm, "end": v(2366.67, 12500) * mm});
            skLineSegment(sketch, "E172.MirrorCS", {"start": v(25966.67, 16300) * mm, "end": v(24766.67, 16300) * mm});
            skLineSegment(sketch, "E173.MirrorCS", {"start": v(15466.67, 13700) * mm, "end": v(14266.67, 13700) * mm});
            skLineSegment(sketch, "E174.MirrorCS", {"start": v(8466.67, 17600) * mm, "end": v(8466.67, 16400) * mm});
            skLineSegment(sketch, "E175.MirrorCS", {"start": v(11966.67, 21500) * mm, "end": v(10766.67, 21500) * mm});
            skLineSegment(sketch, "E176.MirrorCS", {"start": v(10766.67, 21500) * mm, "end": v(10766.67, 20300) * mm});
            skLineSegment(sketch, "E177.MirrorCS", {"start": v(25966.67, 15100) * mm, "end": v(24766.67, 15100) * mm});
            skLineSegment(sketch, "E178.MirrorCS", {"start": v(10566.67, 17600) * mm, "end": v(10566.67, 16400) * mm});
            skLineSegment(sketch, "E179.MirrorCS", {"start": v(12866.67, 21500) * mm, "end": v(12866.67, 20300) * mm});
            skLineSegment(sketch, "E180.MirrorCS", {"start": v(24566.67, 16300) * mm, "end": v(23366.67, 16300) * mm});
            skLineSegment(sketch, "E181.MirrorCS", {"start": v(24566.67, 13700) * mm, "end": v(24566.67, 12500) * mm});
            skLineSegment(sketch, "E182.MirrorCS", {"start": v(21266.67, 13700) * mm, "end": v(21266.67, 12500) * mm});
            skLineSegment(sketch, "E183.MirrorCS", {"start": v(11966.67, 17600) * mm, "end": v(11966.67, 16400) * mm});
            skLineSegment(sketch, "E184.MirrorCS", {"start": v(11966.67, 20200) * mm, "end": v(11966.67, 19000) * mm});
            skLineSegment(sketch, "E185.MirrorCS", {"start": v(9366.67, 20200) * mm, "end": v(9366.67, 19000) * mm});
            skLineSegment(sketch, "E186.MirrorCS", {"start": v(8466.67, 16300) * mm, "end": v(8466.67, 15100) * mm});
            skLineSegment(sketch, "E187.MirrorCS", {"start": v(17566.67, 15000) * mm, "end": v(17566.67, 13800) * mm});
            skLineSegment(sketch, "E188.MirrorCS", {"start": v(22466.67, 12500) * mm, "end": v(21266.67, 12500) * mm});
            skLineSegment(sketch, "E189.MirrorCS", {"start": v(14066.67, 16300) * mm, "end": v(12866.67, 16300) * mm});
            skLineSegment(sketch, "E190.MirrorCS", {"start": v(25966.67, 21500) * mm, "end": v(24766.67, 21500) * mm});
            skLineSegment(sketch, "E191.MirrorCS", {"start": v(23366.67, 21500) * mm, "end": v(19866.67, 21500) * mm, "construction": true});
            skLineSegment(sketch, "E192.MirrorCS", {"start": v(2366.67, 16300) * mm, "end": v(2366.67, 15100) * mm});
            skLineSegment(sketch, "E193.MirrorCS", {"start": v(17566.67, 13800) * mm, "end": v(16366.67, 13800) * mm});
            skLineSegment(sketch, "E194.MirrorCS", {"start": v(3566.67, 15100) * mm, "end": v(2366.67, 15100) * mm});
            skLineSegment(sketch, "E195.MirrorCS", {"start": v(4966.67, 20200) * mm, "end": v(4966.67, 19000) * mm});
            skLineSegment(sketch, "E196.MirrorCS", {"start": v(28166.67, 16300) * mm, "end": v(26966.67, 16300) * mm});
            skLineSegment(sketch, "E197.MirrorCS", {"start": v(11966.67, 16300) * mm, "end": v(11966.67, 15100) * mm});
            skLineSegment(sketch, "E198.MirrorCS", {"start": v(3766.67, 15000) * mm, "end": v(3766.67, 13800) * mm});
            skLineSegment(sketch, "E199.MirrorCS", {"start": v(14066.67, 18900) * mm, "end": v(14066.67, 17700) * mm});
            skLineSegment(sketch, "E200.MirrorCS", {"start": v(18966.67, 21500) * mm, "end": v(17766.67, 21500) * mm});
            skLineSegment(sketch, "E201.MirrorCS", {"start": v(24566.67, 12500) * mm, "end": v(23366.67, 12500) * mm});
            skLineSegment(sketch, "E202.MirrorCS", {"start": v(7266.67, 16300) * mm, "end": v(7266.67, 15100) * mm});
            skLineSegment(sketch, "E203.MirrorCS", {"start": v(14266.67, 17600) * mm, "end": v(14266.67, 16400) * mm});
            skLineSegment(sketch, "E204.MirrorCS", {"start": v(21066.67, 12500) * mm, "end": v(19866.67, 12500) * mm});
            skLineSegment(sketch, "E205.MirrorCS", {"start": v(3766.67, 21500) * mm, "end": v(3766.67, 20300) * mm});
            skLineSegment(sketch, "E206.MirrorCS", {"start": v(7066.67, 18900) * mm, "end": v(7066.67, 17700) * mm});
            skLineSegment(sketch, "E207.MirrorCS", {"start": v(21266.67, 17600) * mm, "end": v(21266.67, 16400) * mm});
            skLineSegment(sketch, "E208.MirrorCS", {"start": v(8466.67, 15000) * mm, "end": v(7266.67, 15000) * mm});
            skLineSegment(sketch, "E209.MirrorCS", {"start": v(14066.67, 15000) * mm, "end": v(14066.67, 13800) * mm});
            skLineSegment(sketch, "E210.MirrorCS", {"start": v(2366.67, 15000) * mm, "end": v(2366.67, 13800) * mm});
            skLineSegment(sketch, "E211.MirrorCS", {"start": v(14066.67, 16300) * mm, "end": v(14066.67, 15100) * mm});
            skLineSegment(sketch, "E212.MirrorCS", {"start": v(10766.67, 15000) * mm, "end": v(10766.67, 13800) * mm});
            skLineSegment(sketch, "E213.MirrorCS", {"start": v(11966.67, 13700) * mm, "end": v(10766.67, 13700) * mm});
            skLineSegment(sketch, "E214.MirrorCS", {"start": v(4966.67, 15000) * mm, "end": v(4966.67, 13800) * mm});
            skLineSegment(sketch, "E215.MirrorCS", {"start": v(10766.67, 20200) * mm, "end": v(10766.67, 19000) * mm});
            skLineSegment(sketch, "E216.MirrorCS", {"start": v(11966.67, 18900) * mm, "end": v(11966.67, 17700) * mm});
            skLineSegment(sketch, "E217.MirrorCS", {"start": v(23366.67, 16300) * mm, "end": v(23366.67, 15100) * mm});
            skLineSegment(sketch, "E218.MirrorCS", {"start": v(3566.67, 13800) * mm, "end": v(2366.67, 13800) * mm});
            skLineSegment(sketch, "E219.MirrorCS", {"start": v(9366.67, 18900) * mm, "end": v(9366.67, 17700) * mm});
            skLineSegment(sketch, "E220.MirrorCS", {"start": v(28166.67, 20200) * mm, "end": v(28166.67, 19000) * mm});
            skLineSegment(sketch, "E221.MirrorCS", {"start": v(17566.67, 13700) * mm, "end": v(17566.67, 12500) * mm});
            skLineSegment(sketch, "E222.MirrorCS", {"start": v(19866.67, 16300) * mm, "end": v(19866.67, 15100) * mm});
            skLineSegment(sketch, "E223.MirrorCS", {"start": v(17566.67, 21500) * mm, "end": v(16366.67, 21500) * mm});
            skLineSegment(sketch, "E224.MirrorCS", {"start": v(10566.67, 18900) * mm, "end": v(10566.67, 17700) * mm});
            skLineSegment(sketch, "E225.MirrorCS", {"start": v(22466.67, 18900) * mm, "end": v(22466.67, 17700) * mm});
            skLineSegment(sketch, "E226.MirrorCS", {"start": v(21066.67, 17700) * mm, "end": v(19866.67, 17700) * mm});
            skLineSegment(sketch, "E227.MirrorCS", {"start": v(18966.67, 13800) * mm, "end": v(17766.67, 13800) * mm});
            skLineSegment(sketch, "E228.MirrorCS", {"start": v(8466.67, 13800) * mm, "end": v(7266.67, 13800) * mm});
            skLineSegment(sketch, "E229.MirrorCS", {"start": v(3766.67, 20200) * mm, "end": v(3766.67, 19000) * mm});
            skLineSegment(sketch, "E230.MirrorCS", {"start": v(24566.67, 21500) * mm, "end": v(23366.67, 21500) * mm});
            skLineSegment(sketch, "E231.MirrorCS", {"start": v(18966.67, 13700) * mm, "end": v(18966.67, 12500) * mm});
            skLineSegment(sketch, "E232.MirrorCS", {"start": v(25966.67, 17600) * mm, "end": v(25966.67, 16400) * mm});
            skLineSegment(sketch, "E233.MirrorCS", {"start": v(26966.67, 16300) * mm, "end": v(26966.67, 15100) * mm});
            skLineSegment(sketch, "E234.MirrorCS", {"start": v(17566.67, 19000) * mm, "end": v(16366.67, 19000) * mm});
            skLineSegment(sketch, "E235.MirrorCS", {"start": v(8466.67, 17700) * mm, "end": v(7266.67, 17700) * mm});
            skLineSegment(sketch, "E236.MirrorCS", {"start": v(14066.67, 17600) * mm, "end": v(12866.67, 17600) * mm});
            skLineSegment(sketch, "E237.MirrorCS", {"start": v(10566.67, 17600) * mm, "end": v(9366.67, 17600) * mm});
            skLineSegment(sketch, "E238.MirrorCS", {"start": v(18966.67, 21500) * mm, "end": v(18966.67, 20300) * mm});
            skLineSegment(sketch, "E239.MirrorCS", {"start": v(10566.67, 15000) * mm, "end": v(9366.67, 15000) * mm});
            skLineSegment(sketch, "E240.MirrorCS", {"start": v(16366.67, 20200) * mm, "end": v(16366.67, 19000) * mm});
            skLineSegment(sketch, "E241.MirrorCS", {"start": v(10566.67, 19000) * mm, "end": v(9366.67, 19000) * mm});
            skLineSegment(sketch, "E242.MirrorCS", {"start": v(25966.67, 17700) * mm, "end": v(24766.67, 17700) * mm});
            skLineSegment(sketch, "E243.MirrorCS", {"start": v(5866.67, 20200) * mm, "end": v(5866.67, 19000) * mm});
            skLineSegment(sketch, "E244.MirrorCS", {"start": v(21066.67, 21500) * mm, "end": v(21066.67, 20300) * mm});
            skLineSegment(sketch, "E245.MirrorCS", {"start": v(28166.67, 21500) * mm, "end": v(26966.67, 21500) * mm});
            skLineSegment(sketch, "E246.MirrorCS", {"start": v(15466.67, 17700) * mm, "end": v(14266.67, 17700) * mm});
            skLineSegment(sketch, "E247.MirrorCS", {"start": v(14066.67, 20300) * mm, "end": v(12866.67, 20300) * mm});
            skLineSegment(sketch, "E248.MirrorCS", {"start": v(28166.67, 15100) * mm, "end": v(26966.67, 15100) * mm});
            skLineSegment(sketch, "E249.MirrorCS", {"start": v(14266.67, 15000) * mm, "end": v(14266.67, 13800) * mm});
            skLineSegment(sketch, "E250.MirrorCS", {"start": v(24766.67, 18900) * mm, "end": v(24766.67, 17700) * mm});
            skLineSegment(sketch, "E251.MirrorCS", {"start": v(15466.67, 17600) * mm, "end": v(15466.67, 16400) * mm});
            skLineSegment(sketch, "E252.MirrorCS", {"start": v(24766.67, 15000) * mm, "end": v(24766.67, 13800) * mm});
            skLineSegment(sketch, "E253.MirrorCS", {"start": v(10766.67, 16300) * mm, "end": v(10766.67, 15100) * mm});
            skLineSegment(sketch, "E254.MirrorCS", {"start": v(17566.67, 13700) * mm, "end": v(16366.67, 13700) * mm});
            skLineSegment(sketch, "E255.MirrorCS", {"start": v(14066.67, 21500) * mm, "end": v(12866.67, 21500) * mm});
            skLineSegment(sketch, "E256.MirrorCS", {"start": v(22466.67, 19000) * mm, "end": v(21266.67, 19000) * mm});
            skLineSegment(sketch, "E257.MirrorCS", {"start": v(21066.67, 16300) * mm, "end": v(21066.67, 15100) * mm});
            skLineSegment(sketch, "E258.MirrorCS", {"start": v(25966.67, 13700) * mm, "end": v(24766.67, 13700) * mm});
            skLineSegment(sketch, "E259.MirrorCS", {"start": v(21266.67, 15000) * mm, "end": v(21266.67, 13800) * mm});
            skLineSegment(sketch, "E260.MirrorCS", {"start": v(14066.67, 15000) * mm, "end": v(12866.67, 15000) * mm});
            skLineSegment(sketch, "E261.MirrorCS", {"start": v(28166.67, 13700) * mm, "end": v(26966.67, 13700) * mm});
            skLineSegment(sketch, "E262.MirrorCS", {"start": v(17566.67, 20200) * mm, "end": v(16366.67, 20200) * mm});
            skLineSegment(sketch, "E263.MirrorCS", {"start": v(7266.67, 13700) * mm, "end": v(7266.67, 12500) * mm});
            skLineSegment(sketch, "E264.MirrorCS", {"start": v(21266.67, 21500) * mm, "end": v(21266.67, 20300) * mm});
            skLineSegment(sketch, "E265.MirrorCS", {"start": v(7066.67, 12500) * mm, "end": v(5866.67, 12500) * mm});
            skLineSegment(sketch, "E266.MirrorCS", {"start": v(3766.67, 16300) * mm, "end": v(3766.67, 15100) * mm});
            skLineSegment(sketch, "E267.MirrorCS", {"start": v(18966.67, 17700) * mm, "end": v(17766.67, 17700) * mm});
            skLineSegment(sketch, "E268.MirrorCS", {"start": v(10566.67, 12500) * mm, "end": v(9366.67, 12500) * mm});
            skLineSegment(sketch, "E269.MirrorCS", {"start": v(17566.67, 16400) * mm, "end": v(16366.67, 16400) * mm});
            skLineSegment(sketch, "E270.MirrorCS", {"start": v(28166.67, 13800) * mm, "end": v(26966.67, 13800) * mm});
            skLineSegment(sketch, "E271.MirrorCS", {"start": v(8466.67, 21500) * mm, "end": v(8466.67, 20300) * mm});
            skLineSegment(sketch, "E272.MirrorCS", {"start": v(10766.67, 13700) * mm, "end": v(10766.67, 12500) * mm});
            skLineSegment(sketch, "E273.MirrorCS", {"start": v(21266.67, 18900) * mm, "end": v(21266.67, 17700) * mm});
            skLineSegment(sketch, "E274.MirrorCS", {"start": v(2366.67, 20200) * mm, "end": v(2366.67, 19000) * mm});
            skLineSegment(sketch, "E275.MirrorCS", {"start": v(11966.67, 18900) * mm, "end": v(10766.67, 18900) * mm});
            skLineSegment(sketch, "E276.MirrorCS", {"start": v(24566.67, 17700) * mm, "end": v(23366.67, 17700) * mm});
            skLineSegment(sketch, "E277.MirrorCS", {"start": v(22466.67, 15000) * mm, "end": v(22466.67, 13800) * mm});
            skLineSegment(sketch, "E278.MirrorCS", {"start": v(24566.67, 16400) * mm, "end": v(23366.67, 16400) * mm});
            skLineSegment(sketch, "E279.MirrorCS", {"start": v(7066.67, 16300) * mm, "end": v(7066.67, 15100) * mm});
            skLineSegment(sketch, "E280.MirrorCS", {"start": v(24566.67, 21500) * mm, "end": v(24566.67, 20300) * mm});
            skLineSegment(sketch, "E281.MirrorCS", {"start": v(21066.67, 17600) * mm, "end": v(21066.67, 16400) * mm});
            skLineSegment(sketch, "E282.MirrorCS", {"start": v(16366.67, 21500) * mm, "end": v(16366.67, 20300) * mm});
            skLineSegment(sketch, "E283.MirrorCS", {"start": v(3566.67, 20200) * mm, "end": v(3566.67, 19000) * mm});
            skLineSegment(sketch, "E284.MirrorCS", {"start": v(23366.67, 17600) * mm, "end": v(23366.67, 16400) * mm});
            skLineSegment(sketch, "E285.MirrorCS", {"start": v(4966.67, 16300) * mm, "end": v(4966.67, 15100) * mm});
            skLineSegment(sketch, "E286.MirrorCS", {"start": v(3566.67, 19000) * mm, "end": v(2366.67, 19000) * mm});
            skLineSegment(sketch, "E287.MirrorCS", {"start": v(11966.67, 13700) * mm, "end": v(11966.67, 12500) * mm});
            skLineSegment(sketch, "E288.MirrorCS", {"start": v(28166.67, 15000) * mm, "end": v(28166.67, 13800) * mm});
            skLineSegment(sketch, "E289.MirrorCS", {"start": v(17766.67, 18900) * mm, "end": v(17766.67, 17700) * mm});
            skLineSegment(sketch, "E290.MirrorCS", {"start": v(11966.67, 15000) * mm, "end": v(11966.67, 13800) * mm});
            skLineSegment(sketch, "E291.MirrorCS", {"start": v(28166.67, 18900) * mm, "end": v(26966.67, 18900) * mm});
            skLineSegment(sketch, "E292.MirrorCS", {"start": v(7066.67, 19000) * mm, "end": v(5866.67, 19000) * mm});
            skLineSegment(sketch, "E293.MirrorCS", {"start": v(15466.67, 16300) * mm, "end": v(14266.67, 16300) * mm});
            skLineSegment(sketch, "E294.MirrorCS", {"start": v(22466.67, 17700) * mm, "end": v(21266.67, 17700) * mm});
            skLineSegment(sketch, "E295.MirrorCS", {"start": v(3766.67, 17600) * mm, "end": v(3766.67, 16400) * mm});
            skLineSegment(sketch, "E296.MirrorCS", {"start": v(14266.67, 13700) * mm, "end": v(14266.67, 12500) * mm});
            skLineSegment(sketch, "E297.MirrorCS", {"start": v(4966.67, 17600) * mm, "end": v(4966.67, 16400) * mm});
            skLineSegment(sketch, "E298.MirrorCS", {"start": v(10566.67, 16400) * mm, "end": v(9366.67, 16400) * mm});
            skLineSegment(sketch, "E299.MirrorCS", {"start": v(3566.67, 17600) * mm, "end": v(3566.67, 16400) * mm});
            skLineSegment(sketch, "E300.MirrorCS", {"start": v(14066.67, 12500) * mm, "end": v(12866.67, 12500) * mm});
            skLineSegment(sketch, "E301.MirrorCS", {"start": v(24566.67, 13800) * mm, "end": v(23366.67, 13800) * mm});
            skLineSegment(sketch, "E302.MirrorCS", {"start": v(7266.67, 15000) * mm, "end": v(7266.67, 13800) * mm});
            skLineSegment(sketch, "E303.MirrorCS", {"start": v(10566.67, 17700) * mm, "end": v(9366.67, 17700) * mm});
            skLineSegment(sketch, "E304.MirrorCS", {"start": v(5866.67, 16300) * mm, "end": v(5866.67, 15100) * mm});
            skLineSegment(sketch, "E305.MirrorCS", {"start": v(15466.67, 17600) * mm, "end": v(14266.67, 17600) * mm});
            skLineSegment(sketch, "E306.MirrorCS", {"start": v(10566.67, 20300) * mm, "end": v(9366.67, 20300) * mm});
            skLineSegment(sketch, "E307.MirrorCS", {"start": v(4966.67, 13700) * mm, "end": v(3766.67, 13700) * mm});
            skLineSegment(sketch, "E308.MirrorCS", {"start": v(15466.67, 21500) * mm, "end": v(15466.67, 20300) * mm});
            skLineSegment(sketch, "E309.MirrorCS", {"start": v(25966.67, 16300) * mm, "end": v(25966.67, 15100) * mm});
            skLineSegment(sketch, "E310.MirrorCS", {"start": v(24566.67, 13700) * mm, "end": v(23366.67, 13700) * mm});
            skLineSegment(sketch, "E311.MirrorCS", {"start": v(4966.67, 20200) * mm, "end": v(3766.67, 20200) * mm});
            skLineSegment(sketch, "E312.MirrorCS", {"start": v(15466.67, 12500) * mm, "end": v(14266.67, 12500) * mm});
            skLineSegment(sketch, "E313.MirrorCS", {"start": v(14066.67, 20200) * mm, "end": v(14066.67, 19000) * mm});
            skLineSegment(sketch, "E314.MirrorCS", {"start": v(24566.67, 15100) * mm, "end": v(23366.67, 15100) * mm});
            skLineSegment(sketch, "E315.MirrorCS", {"start": v(4966.67, 21500) * mm, "end": v(3766.67, 21500) * mm});
            skLineSegment(sketch, "E316.MirrorCS", {"start": v(15466.67, 21500) * mm, "end": v(14266.67, 21500) * mm});
            skLineSegment(sketch, "E317.MirrorCS", {"start": v(15466.67, 13700) * mm, "end": v(15466.67, 12500) * mm});
            skLineSegment(sketch, "E318.MirrorCS", {"start": v(10566.67, 16300) * mm, "end": v(10566.67, 15100) * mm});
            skLineSegment(sketch, "E319.MirrorCS", {"start": v(3766.67, 18900) * mm, "end": v(3766.67, 17700) * mm});
            skLineSegment(sketch, "E320.MirrorCS", {"start": v(24566.67, 20200) * mm, "end": v(24566.67, 19000) * mm});
            skLineSegment(sketch, "E321.MirrorCS", {"start": v(14066.67, 20200) * mm, "end": v(12866.67, 20200) * mm});
            skLineSegment(sketch, "E322.MirrorCS", {"start": v(4966.67, 16400) * mm, "end": v(3766.67, 16400) * mm});
            skLineSegment(sketch, "E323.MirrorCS", {"start": v(11966.67, 20200) * mm, "end": v(10766.67, 20200) * mm});
            skLineSegment(sketch, "E324.MirrorCS", {"start": v(28166.67, 20200) * mm, "end": v(26966.67, 20200) * mm});
            skLineSegment(sketch, "E325.MirrorCS", {"start": v(22466.67, 20300) * mm, "end": v(21266.67, 20300) * mm});
            skLineSegment(sketch, "E326.MirrorCS", {"start": v(10566.67, 18900) * mm, "end": v(9366.67, 18900) * mm});
            skLineSegment(sketch, "E327.MirrorCS", {"start": v(15466.67, 20300) * mm, "end": v(14266.67, 20300) * mm});
            skLineSegment(sketch, "E328.MirrorCS", {"start": v(16366.67, 16300) * mm, "end": v(16366.67, 15100) * mm});
            skLineSegment(sketch, "E329.MirrorCS", {"start": v(28166.67, 16400) * mm, "end": v(26966.67, 16400) * mm});
            skLineSegment(sketch, "E330.MirrorCS", {"start": v(18966.67, 18900) * mm, "end": v(18966.67, 17700) * mm});
            skLineSegment(sketch, "E331.MirrorCS", {"start": v(7066.67, 16300) * mm, "end": v(5866.67, 16300) * mm});
            skLineSegment(sketch, "E332.MirrorCS", {"start": v(4966.67, 13800) * mm, "end": v(3766.67, 13800) * mm});
            skLineSegment(sketch, "E333.MirrorCS", {"start": v(11966.67, 17600) * mm, "end": v(10766.67, 17600) * mm});
            skLineSegment(sketch, "E334.MirrorCS", {"start": v(12866.67, 15000) * mm, "end": v(12866.67, 13800) * mm});
            skLineSegment(sketch, "E335.MirrorCS", {"start": v(21066.67, 20300) * mm, "end": v(19866.67, 20300) * mm});
            skLineSegment(sketch, "E336.MirrorCS", {"start": v(10566.67, 13700) * mm, "end": v(10566.67, 12500) * mm});
            skLineSegment(sketch, "E337.MirrorCS", {"start": v(21266.67, 16300) * mm, "end": v(21266.67, 15100) * mm});
            skLineSegment(sketch, "E338.MirrorCS", {"start": v(11966.67, 15100) * mm, "end": v(10766.67, 15100) * mm});
            skLineSegment(sketch, "E339.MirrorCS", {"start": v(4966.67, 20300) * mm, "end": v(3766.67, 20300) * mm});
            skLineSegment(sketch, "E340.MirrorCS", {"start": v(9366.67, 16300) * mm, "end": v(9366.67, 15100) * mm});
            skLineSegment(sketch, "E341.MirrorCS", {"start": v(14066.67, 16400) * mm, "end": v(12866.67, 16400) * mm});
            skLineSegment(sketch, "E342.MirrorCS", {"start": v(17566.67, 20200) * mm, "end": v(17566.67, 19000) * mm});
            skLineSegment(sketch, "E343.MirrorCS", {"start": v(19866.67, 17600) * mm, "end": v(19866.67, 16400) * mm});
            skLineSegment(sketch, "E344.MirrorCS", {"start": v(15466.67, 18900) * mm, "end": v(15466.67, 17700) * mm});
            skLineSegment(sketch, "E345.MirrorCS", {"start": v(8466.67, 13700) * mm, "end": v(7266.67, 13700) * mm});
            skLineSegment(sketch, "E346.MirrorCS", {"start": v(23366.67, 15000) * mm, "end": v(19866.67, 15000) * mm, "construction": true});
            skLineSegment(sketch, "E347.MirrorCS", {"start": v(11966.67, 16400) * mm, "end": v(10766.67, 16400) * mm});
            skLineSegment(sketch, "E348.MirrorCS", {"start": v(23366.67, 20200) * mm, "end": v(19866.67, 20200) * mm, "construction": true});
            skLineSegment(sketch, "E349.MirrorCS", {"start": v(3566.67, 16400) * mm, "end": v(2366.67, 16400) * mm});
            skLineSegment(sketch, "E350.MirrorCS", {"start": v(5866.67, 13700) * mm, "end": v(5866.67, 12500) * mm});
            skLineSegment(sketch, "E351.MirrorCS", {"start": v(7066.67, 20300) * mm, "end": v(5866.67, 20300) * mm});
            skLineSegment(sketch, "E352.MirrorCS", {"start": v(8466.67, 21500) * mm, "end": v(7266.67, 21500) * mm});
            skLineSegment(sketch, "E353.MirrorCS", {"start": v(18966.67, 20200) * mm, "end": v(18966.67, 19000) * mm});
            skLineSegment(sketch, "E354.MirrorCS", {"start": v(23366.67, 16300) * mm, "end": v(19866.67, 16300) * mm, "construction": true});
            skLineSegment(sketch, "E355.MirrorCS", {"start": v(7266.67, 17600) * mm, "end": v(7266.67, 16400) * mm});
            skLineSegment(sketch, "E356.MirrorCS", {"start": v(17566.67, 17600) * mm, "end": v(17566.67, 16400) * mm});
            skLineSegment(sketch, "E357.MirrorCS", {"start": v(25966.67, 15000) * mm, "end": v(24766.67, 15000) * mm});
            skLineSegment(sketch, "E358.MirrorCS", {"start": v(10566.67, 13800) * mm, "end": v(9366.67, 13800) * mm});
            skLineSegment(sketch, "E359.MirrorCS", {"start": v(25966.67, 18900) * mm, "end": v(24766.67, 18900) * mm});
            skLineSegment(sketch, "E360.MirrorCS", {"start": v(14066.67, 13700) * mm, "end": v(14066.67, 12500) * mm});
            skLineSegment(sketch, "E361.MirrorCS", {"start": v(18966.67, 16300) * mm, "end": v(18966.67, 15100) * mm});
            skLineSegment(sketch, "E362.MirrorCS", {"start": v(17566.67, 21500) * mm, "end": v(17566.67, 20300) * mm});
            skLineSegment(sketch, "E363.MirrorCS", {"start": v(14066.67, 13700) * mm, "end": v(12866.67, 13700) * mm});
            skLineSegment(sketch, "E364.MirrorCS", {"start": v(23366.67, 18900) * mm, "end": v(19866.67, 18900) * mm, "construction": true});
            skLineSegment(sketch, "E365.MirrorCS", {"start": v(28166.67, 13700) * mm, "end": v(28166.67, 12500) * mm});
            skLineSegment(sketch, "E366.MirrorCS", {"start": v(4966.67, 15000) * mm, "end": v(3766.67, 15000) * mm});
            skLineSegment(sketch, "E367.MirrorCS", {"start": v(7266.67, 21500) * mm, "end": v(7266.67, 20300) * mm});
            skLineSegment(sketch, "E368.MirrorCS", {"start": v(4966.67, 17700) * mm, "end": v(3766.67, 17700) * mm});
            skLineSegment(sketch, "E369.MirrorCS", {"start": v(14066.67, 13800) * mm, "end": v(12866.67, 13800) * mm});
            skLineSegment(sketch, "E370.MirrorCS", {"start": v(8466.67, 15100) * mm, "end": v(7266.67, 15100) * mm});
            skLineSegment(sketch, "E371.MirrorCS", {"start": v(18966.67, 17600) * mm, "end": v(18966.67, 16400) * mm});
            skLineSegment(sketch, "E372.MirrorCS", {"start": v(14066.67, 19000) * mm, "end": v(12866.67, 19000) * mm});
            skLineSegment(sketch, "E373.MirrorCS", {"start": v(15466.67, 16300) * mm, "end": v(15466.67, 15100) * mm});
            skLineSegment(sketch, "E374.MirrorCS", {"start": v(5866.67, 18900) * mm, "end": v(5866.67, 17700) * mm});
            skLineSegment(sketch, "E375.MirrorCS", {"start": v(28166.67, 18900) * mm, "end": v(28166.67, 17700) * mm});
            skLineSegment(sketch, "E376.MirrorCS", {"start": v(11966.67, 13800) * mm, "end": v(10766.67, 13800) * mm});
            skLineSegment(sketch, "E377.MirrorCS", {"start": v(28166.67, 17700) * mm, "end": v(26966.67, 17700) * mm});
            skLineSegment(sketch, "E378.MirrorCS", {"start": v(7066.67, 20200) * mm, "end": v(5866.67, 20200) * mm});
            skLineSegment(sketch, "E379.MirrorCS", {"start": v(24766.67, 13700) * mm, "end": v(24766.67, 12500) * mm});
            skLineSegment(sketch, "E380.MirrorCS", {"start": v(10566.67, 20200) * mm, "end": v(9366.67, 20200) * mm});
            skLineSegment(sketch, "E381.MirrorCS", {"start": v(25966.67, 15000) * mm, "end": v(25966.67, 13800) * mm});
            skLineSegment(sketch, "E382.MirrorCS", {"start": v(17566.67, 20300) * mm, "end": v(16366.67, 20300) * mm});
            skLineSegment(sketch, "E383.MirrorCS", {"start": v(18966.67, 13700) * mm, "end": v(17766.67, 13700) * mm});
            skLineSegment(sketch, "E384.MirrorCS", {"start": v(10566.67, 15000) * mm, "end": v(10566.67, 13800) * mm});
            skLineSegment(sketch, "E385.MirrorCS", {"start": v(28166.67, 16300) * mm, "end": v(28166.67, 15100) * mm});
            skLineSegment(sketch, "E386.MirrorCS", {"start": v(24566.67, 16300) * mm, "end": v(24566.67, 15100) * mm});
            skLineSegment(sketch, "E387.MirrorCS", {"start": v(14066.67, 18900) * mm, "end": v(12866.67, 18900) * mm});
            skLineSegment(sketch, "E388.MirrorCS", {"start": v(4966.67, 12500) * mm, "end": v(3766.67, 12500) * mm});
            skLineSegment(sketch, "E389.MirrorCS", {"start": v(3566.67, 20300) * mm, "end": v(2366.67, 20300) * mm});
            skLineSegment(sketch, "E390.MirrorCS", {"start": v(2366.67, 18900) * mm, "end": v(2366.67, 17700) * mm});
            skLineSegment(sketch, "E391.MirrorCS", {"start": v(15466.67, 13800) * mm, "end": v(14266.67, 13800) * mm});
            skLineSegment(sketch, "E392.MirrorCS", {"start": v(22466.67, 21500) * mm, "end": v(22466.67, 20300) * mm});
            skLineSegment(sketch, "E393.MirrorCS", {"start": v(7066.67, 21500) * mm, "end": v(7066.67, 20300) * mm});
            skLineSegment(sketch, "E394.MirrorCS", {"start": v(8466.67, 20200) * mm, "end": v(8466.67, 19000) * mm});
            skLineSegment(sketch, "E395.MirrorCS", {"start": v(16366.67, 18900) * mm, "end": v(16366.67, 17700) * mm});
            skLineSegment(sketch, "E396.MirrorCS", {"start": v(24766.67, 17600) * mm, "end": v(24766.67, 16400) * mm});
            skLineSegment(sketch, "E397.MirrorCS", {"start": v(17766.67, 21500) * mm, "end": v(17766.67, 20300) * mm});
            skLineSegment(sketch, "E398.MirrorCS", {"start": v(15466.67, 20200) * mm, "end": v(15466.67, 19000) * mm});
            skLineSegment(sketch, "E399.MirrorCS", {"start": v(23366.67, 13700) * mm, "end": v(23366.67, 12500) * mm});
            skLineSegment(sketch, "E400.MirrorCS", {"start": v(25966.67, 20200) * mm, "end": v(24766.67, 20200) * mm});
            skLineSegment(sketch, "E401.MirrorCS", {"start": v(4966.67, 17600) * mm, "end": v(3766.67, 17600) * mm});
            skLineSegment(sketch, "E402.MirrorCS", {"start": v(26966.67, 20300) * mm, "end": v(26966.67, 19000) * mm, "construction": true});
            skLineSegment(sketch, "E403.MirrorCS", {"start": v(17566.67, 15000) * mm, "end": v(16366.67, 15000) * mm});
            skLineSegment(sketch, "E404.MirrorCS", {"start": v(4966.67, 16300) * mm, "end": v(3766.67, 16300) * mm});
            skLineSegment(sketch, "E405.MirrorCS", {"start": v(10566.67, 15100) * mm, "end": v(9366.67, 15100) * mm});
            skLineSegment(sketch, "E406.MirrorCS", {"start": v(7266.67, 20200) * mm, "end": v(7266.67, 19000) * mm});
            skLineSegment(sketch, "E407.MirrorCS", {"start": v(4966.67, 18900) * mm, "end": v(4966.67, 17700) * mm});
            skLineSegment(sketch, "E408.MirrorCS", {"start": v(25966.67, 21500) * mm, "end": v(25966.67, 20300) * mm});
            skLineSegment(sketch, "E409.MirrorCS", {"start": v(3566.67, 13700) * mm, "end": v(2366.67, 13700) * mm});
            skLineSegment(sketch, "E410.MirrorCS", {"start": v(18966.67, 15000) * mm, "end": v(17766.67, 15000) * mm});
            skLineSegment(sketch, "E411.MirrorCS", {"start": v(17566.67, 12500) * mm, "end": v(16366.67, 12500) * mm});
            skLineSegment(sketch, "E412.MirrorCS", {"start": v(22466.67, 13800) * mm, "end": v(21266.67, 13800) * mm});
            skLineSegment(sketch, "E413.MirrorCS", {"start": v(25966.67, 18900) * mm, "end": v(25966.67, 17700) * mm});
            skLineSegment(sketch, "E414.MirrorCS", {"start": v(23366.67, 15000) * mm, "end": v(23366.67, 13800) * mm});
            skLineSegment(sketch, "E415.MirrorCS", {"start": v(3566.67, 21500) * mm, "end": v(3566.67, 20300) * mm});
            skLineSegment(sketch, "E416.MirrorCS", {"start": v(24566.67, 18900) * mm, "end": v(24566.67, 17700) * mm});
            skLineSegment(sketch, "E417.MirrorCS", {"start": v(8466.67, 15000) * mm, "end": v(8466.67, 13800) * mm});
            skLineSegment(sketch, "E418.MirrorCS", {"start": v(3566.67, 18900) * mm, "end": v(2366.67, 18900) * mm});
            skLineSegment(sketch, "E419.MirrorCS", {"start": v(10566.67, 20200) * mm, "end": v(10566.67, 19000) * mm});
            skLineSegment(sketch, "E420.MirrorCS", {"start": v(3566.67, 20200) * mm, "end": v(2366.67, 20200) * mm});
            skLineSegment(sketch, "E421.MirrorCS", {"start": v(28166.67, 17600) * mm, "end": v(28166.67, 16400) * mm});
            skLineSegment(sketch, "E422.MirrorCS", {"start": v(14266.67, 18900) * mm, "end": v(14266.67, 17700) * mm});
            skLineSegment(sketch, "E423.MirrorCS", {"start": v(17566.67, 18900) * mm, "end": v(16366.67, 18900) * mm});
            skLineSegment(sketch, "E424.MirrorCS", {"start": v(11966.67, 15000) * mm, "end": v(10766.67, 15000) * mm});
            skLineSegment(sketch, "E425.MirrorCS", {"start": v(23366.67, 21500) * mm, "end": v(23366.67, 20300) * mm});
            skLineSegment(sketch, "E426.MirrorCS", {"start": v(23366.67, 20200) * mm, "end": v(23366.67, 19000) * mm});
            skLineSegment(sketch, "E427.MirrorCS", {"start": v(21066.67, 15100) * mm, "end": v(19866.67, 15100) * mm});
            skLineSegment(sketch, "E428.MirrorCS", {"start": v(23366.67, 18900) * mm, "end": v(23366.67, 17700) * mm});
            skLineSegment(sketch, "E429.MirrorCS", {"start": v(7066.67, 13800) * mm, "end": v(5866.67, 13800) * mm});
            skLineSegment(sketch, "E430.MirrorCS", {"start": v(15466.67, 20200) * mm, "end": v(14266.67, 20200) * mm});
            skLineSegment(sketch, "E431.MirrorCS", {"start": v(9366.67, 15000) * mm, "end": v(9366.67, 13800) * mm});
            skLineSegment(sketch, "E432.MirrorCS", {"start": v(21266.67, 20200) * mm, "end": v(21266.67, 19000) * mm});
            skLineSegment(sketch, "E433.MirrorCS", {"start": v(8466.67, 13700) * mm, "end": v(8466.67, 12500) * mm});
            skLineSegment(sketch, "E434.MirrorCS", {"start": v(10766.67, 17600) * mm, "end": v(10766.67, 16400) * mm});
            skLineSegment(sketch, "E435.MirrorCS", {"start": v(4966.67, 18900) * mm, "end": v(3766.67, 18900) * mm});
            skLineSegment(sketch, "E436.MirrorCS", {"start": v(8466.67, 18900) * mm, "end": v(7266.67, 18900) * mm});
            skLineSegment(sketch, "E437.MirrorCS", {"start": v(10566.67, 21500) * mm, "end": v(10566.67, 20300) * mm});
            skLineSegment(sketch, "E438.MirrorCS", {"start": v(9366.67, 13700) * mm, "end": v(9366.67, 12500) * mm});
            skLineSegment(sketch, "E439.MirrorCS", {"start": v(17766.67, 13700) * mm, "end": v(17766.67, 12500) * mm});
            skLineSegment(sketch, "E440.MirrorCS", {"start": v(24766.67, 16300) * mm, "end": v(24766.67, 15100) * mm});
            skLineSegment(sketch, "E441.MirrorCS", {"start": v(5866.67, 15000) * mm, "end": v(5866.67, 13800) * mm});
            skLineSegment(sketch, "E442.MirrorCS", {"start": v(3766.67, 13700) * mm, "end": v(3766.67, 12500) * mm});
            skLineSegment(sketch, "E443.MirrorCS", {"start": v(14266.67, 20200) * mm, "end": v(14266.67, 19000) * mm});
            skLineSegment(sketch, "E444.MirrorCS", {"start": v(18966.67, 16400) * mm, "end": v(17766.67, 16400) * mm});
            skLineSegment(sketch, "E445.MirrorCS", {"start": v(18966.67, 20300) * mm, "end": v(17766.67, 20300) * mm});
            skLineSegment(sketch, "E446.MirrorCS", {"start": v(17766.67, 15000) * mm, "end": v(17766.67, 13800) * mm});
            skLineSegment(sketch, "E447.MirrorCS", {"start": v(21066.67, 18900) * mm, "end": v(21066.67, 17700) * mm});
            skLineSegment(sketch, "E448.MirrorCS", {"start": v(8466.67, 12500) * mm, "end": v(7266.67, 12500) * mm});
            skLineSegment(sketch, "E449.MirrorCS", {"start": v(10566.67, 21500) * mm, "end": v(9366.67, 21500) * mm});
            skLineSegment(sketch, "E450.MirrorCS", {"start": v(24566.67, 20300) * mm, "end": v(23366.67, 20300) * mm});
            skLineSegment(sketch, "E451.MirrorCS", {"start": v(24566.67, 17600) * mm, "end": v(24566.67, 16400) * mm});
            skLineSegment(sketch, "E452.MirrorCS", {"start": v(23366.67, 17600) * mm, "end": v(19866.67, 17600) * mm, "construction": true});
            skLineSegment(sketch, "E453.MirrorCS", {"start": v(24566.67, 18900) * mm, "end": v(23366.67, 18900) * mm});
            skLineSegment(sketch, "E454.MirrorCS", {"start": v(4966.67, 13700) * mm, "end": v(4966.67, 12500) * mm});
            skLineSegment(sketch, "E455.MirrorCS", {"start": v(24566.67, 15000) * mm, "end": v(24566.67, 13800) * mm});
            skLineSegment(sketch, "E456.MirrorCS", {"start": v(17766.67, 16300) * mm, "end": v(17766.67, 15100) * mm});
            skLineSegment(sketch, "E457.MirrorCS", {"start": v(12866.67, 18900) * mm, "end": v(12866.67, 17700) * mm});
            skLineSegment(sketch, "E458.MirrorCS", {"start": v(14066.67, 21500) * mm, "end": v(14066.67, 20300) * mm});
            skLineSegment(sketch, "E459.MirrorCS", {"start": v(4966.67, 21500) * mm, "end": v(4966.67, 20300) * mm});
            skLineSegment(sketch, "E460.MirrorCS", {"start": v(8466.67, 18900) * mm, "end": v(8466.67, 17700) * mm});
            skLineSegment(sketch, "E461.MirrorCS", {"start": v(8466.67, 20300) * mm, "end": v(7266.67, 20300) * mm});
            skLineSegment(sketch, "E462.MirrorCS", {"start": v(7066.67, 18900) * mm, "end": v(5866.67, 18900) * mm});
            skLineSegment(sketch, "E463.MirrorCS", {"start": v(25966.67, 12500) * mm, "end": v(24766.67, 12500) * mm});
            skLineSegment(sketch, "E464.MirrorCS", {"start": v(25966.67, 20300) * mm, "end": v(24766.67, 20300) * mm});
            skLineSegment(sketch, "E465.MirrorCS", {"start": v(22466.67, 17600) * mm, "end": v(22466.67, 16400) * mm});
            skLineSegment(sketch, "E466.MirrorCS", {"start": v(16366.67, 13700) * mm, "end": v(16366.67, 12500) * mm});
            skLineSegment(sketch, "E467.MirrorCS", {"start": v(21066.67, 19000) * mm, "end": v(19866.67, 19000) * mm});
            skLineSegment(sketch, "E468.MirrorCS", {"start": v(11966.67, 19000) * mm, "end": v(10766.67, 19000) * mm});
            skLineSegment(sketch, "E469.MirrorCS", {"start": v(7066.67, 17700) * mm, "end": v(5866.67, 17700) * mm});
            skLineSegment(sketch, "E470.MirrorCS", {"start": v(25966.67, 20200) * mm, "end": v(25966.67, 19000) * mm});
            skLineSegment(sketch, "E471.MirrorCS", {"start": v(3566.67, 16300) * mm, "end": v(2366.67, 16300) * mm});
            skLineSegment(sketch, "E472.MirrorCS", {"start": v(15466.67, 19000) * mm, "end": v(14266.67, 19000) * mm});
            skLineSegment(sketch, "E473.MirrorCS", {"start": v(17566.67, 17600) * mm, "end": v(16366.67, 17600) * mm});
            skLineSegment(sketch, "E474.MirrorCS", {"start": v(18966.67, 18900) * mm, "end": v(17766.67, 18900) * mm});
            skLineSegment(sketch, "E475.MirrorCS", {"start": v(28166.67, 12500) * mm, "end": v(26966.67, 12500) * mm});
            skLineSegment(sketch, "E476.MirrorCS", {"start": v(2366.67, 13700) * mm, "end": v(2366.67, 12500) * mm});
            skLineSegment(sketch, "E477.MirrorCS", {"start": v(28166.67, 17600) * mm, "end": v(26966.67, 17600) * mm});
            skLineSegment(sketch, "E478.MirrorCS", {"start": v(7066.67, 15000) * mm, "end": v(7066.67, 13800) * mm});
            skLineSegment(sketch, "E479.MirrorCS", {"start": v(15466.67, 16400) * mm, "end": v(14266.67, 16400) * mm});
            skLineSegment(sketch, "E480.MirrorCS", {"start": v(25966.67, 13700) * mm, "end": v(25966.67, 12500) * mm});
            skLineSegment(sketch, "E481.MirrorCS", {"start": v(14066.67, 17700) * mm, "end": v(12866.67, 17700) * mm});
            skLineSegment(sketch, "E482.MirrorCS", {"start": v(26966.67, 21500) * mm, "end": v(26966.67, 20300) * mm});
            skLineSegment(sketch, "E483.MirrorCS", {"start": v(11966.67, 20300) * mm, "end": v(10766.67, 20300) * mm});
            skLineSegment(sketch, "E484.MirrorCS", {"start": v(9366.67, 21500) * mm, "end": v(9366.67, 20300) * mm});
            skLineSegment(sketch, "E485.MirrorCS", {"start": v(16366.67, 17600) * mm, "end": v(16366.67, 16400) * mm});
            skLineSegment(sketch, "E486.MirrorCS", {"start": v(25966.67, 13800) * mm, "end": v(24766.67, 13800) * mm});
            skSolve(sketch);
        }
        {
            var Q0;
            Q0 = qSketchRegion(id + "F5", true);
            extrude(context, id + "F6", {"entities" : qUnion([Q0]), "operationType" : NewBodyOperationType.ADD, "depth" : 1000 * mm, "offsetDistance" : 25 * mm});
        }
    });
